FCSTD DOCUMENT  (FreeCAD 0.16R5861 (Git))
Label: extruder_mount_TAZ6_0.8
License: CC-BY 3.0
LicenseURL: http://creativecommons.org/licenses/by/3.0/
objects: Sketcher::SketchObject×85, PartDesign::Pocket×58, PartDesign::Pad×27, PartDesign::Chamfer×23, PartDesign::Fillet×17, Part::Feature×7
note: 302 computed .brp shape members not serialized (recipe doc carries the construction recipe); baked Part::Feature solids carry a one-line shape summary decoded from their .brp

FEATURE [Sketcher::SketchObject] Sketch
  sketch-geometry (38):
    g0: LineSegment [constr] StartX=-50 StartY=41.5 StartZ=0 EndX=50 EndY=41.5 EndZ=0
    g1: LineSegment StartX=50 StartY=41.5 StartZ=0 EndX=50 EndY=-41.5 EndZ=0
    g2: LineSegment [constr] StartX=50 StartY=-41.5 StartZ=0 EndX=-50 EndY=-41.5 EndZ=0
    g3: LineSegment StartX=-50 StartY=-41.5 StartZ=0 EndX=-50 EndY=41.5 EndZ=0
    g4: LineSegment StartX=-44 StartY=-41.5 StartZ=0 EndX=-45.4867 EndY=-53.8036 EndZ=0
    g5: LineSegment StartX=44 StartY=-41.5 StartZ=0 EndX=45.4867 EndY=-53.8036 EndZ=0
    g6: LineSegment StartX=45.4867 StartY=-53.8036 StartZ=0 EndX=0 EndY=-59.3 EndZ=0
    g7: LineSegment StartX=0 StartY=-59.3 StartZ=0 EndX=-45.4867 EndY=-53.8036 EndZ=0
    g8: LineSegment StartX=-50 StartY=-41.5 StartZ=0 EndX=-44 EndY=-41.5 EndZ=0
    g9: LineSegment StartX=44 StartY=-41.5 StartZ=0 EndX=50 EndY=-41.5 EndZ=0
    g10: LineSegment [constr] StartX=12.5 StartY=41.5 StartZ=0 EndX=12.5 EndY=51.1 EndZ=0
    g11: LineSegment [constr] StartX=12.5 StartY=51.1 StartZ=0 EndX=-12.5 EndY=51.1 EndZ=0
    g12: LineSegment [constr] StartX=-12.5 StartY=51.1 StartZ=0 EndX=-12.5 EndY=41.5 EndZ=0
    g13: ArcOfCircle CenterX=0 CenterY=44.7952 CenterZ=0 NormalX=0 NormalY=0 NormalZ=1 Radius=14 StartAngle=0.467146 EndAngle=2.67445
    g14: LineSegment [constr] StartX=-2.1 StartY=52.1 StartZ=0 EndX=2.1 EndY=52.1 EndZ=0
    g15: LineSegment StartX=2.1 StartY=52.1 StartZ=0 EndX=2.1 EndY=49.1 EndZ=0
    g16: LineSegment [constr] StartX=2.1 StartY=49.1 StartZ=0 EndX=-2.1 EndY=49.1 EndZ=0
    g17: LineSegment StartX=-2.1 StartY=49.1 StartZ=0 EndX=-2.1 EndY=52.1 EndZ=0
    g18: ArcOfCircle CenterX=0 CenterY=52.1 CenterZ=0 NormalX=0 NormalY=0 NormalZ=1 Radius=2.1 StartAngle=0 EndAngle=3.14159
    g19: ArcOfCircle CenterX=0 CenterY=49.1 CenterZ=0 NormalX=0 NormalY=0 NormalZ=1 Radius=2.1 StartAngle=3.14159 EndAngle=6.28319
    g20: ArcOfCircle CenterX=-15.5 CenterY=44.5 CenterZ=0 NormalX=0 NormalY=0 NormalZ=1 Radius=3 StartAngle=4.71239 EndAngle=6.28319
    g21: ArcOfCircle CenterX=15.5 CenterY=44.5 CenterZ=0 NormalX=0 NormalY=0 NormalZ=1 Radius=3 StartAngle=3.14159 EndAngle=4.71239
    g22: LineSegment StartX=-50 StartY=41.5 StartZ=0 EndX=-15.5 EndY=41.5 EndZ=0
    g23: LineSegment StartX=15.5 StartY=41.5 StartZ=0 EndX=50 EndY=41.5 EndZ=0
    g24: LineSegment StartX=-12.5 StartY=51.1 StartZ=0 EndX=-12.5 EndY=44.5 EndZ=0
    g25: LineSegment StartX=12.5 StartY=51.1 StartZ=0 EndX=12.5 EndY=44.5 EndZ=0
    g26: LineSegment [constr] StartX=-36 StartY=-13.5 StartZ=0 EndX=-8 EndY=-13.5 EndZ=0
    g27: LineSegment StartX=-8 StartY=-13.5 StartZ=0 EndX=-8 EndY=16.5 EndZ=0
    g28: LineSegment [constr] StartX=-8 StartY=16.5 StartZ=0 EndX=-36 EndY=16.5 EndZ=0
    g29: LineSegment StartX=-36 StartY=16.5 StartZ=0 EndX=-36 EndY=-13.5 EndZ=0
    g30: LineSegment [constr] StartX=8 StartY=16.5 StartZ=0 EndX=36 EndY=16.5 EndZ=0
    g31: LineSegment StartX=36 StartY=16.5 StartZ=0 EndX=36 EndY=-13.5 EndZ=0
    g32: LineSegment [constr] StartX=36 StartY=-13.5 StartZ=0 EndX=8 EndY=-13.5 EndZ=0
    g33: LineSegment StartX=8 StartY=-13.5 StartZ=0 EndX=8 EndY=16.5 EndZ=0
    g34: ArcOfCircle CenterX=-22 CenterY=16.5 CenterZ=0 NormalX=0 NormalY=0 NormalZ=1 Radius=14 StartAngle=0 EndAngle=3.14159
    g35: ArcOfCircle CenterX=22 CenterY=16.5 CenterZ=0 NormalX=0 NormalY=0 NormalZ=1 Radius=14 StartAngle=0 EndAngle=3.14159
    g36: ArcOfCircle CenterX=-22 CenterY=-13.5 CenterZ=0 NormalX=0 NormalY=0 NormalZ=1 Radius=14 StartAngle=3.14159 EndAngle=6.28319
    g37: ArcOfCircle CenterX=22 CenterY=-13.5 CenterZ=0 NormalX=0 NormalY=0 NormalZ=1 Radius=14 StartAngle=3.14159 EndAngle=6.28319
  constraints (114):
    c: Coincident(g0,g1)
    c: Coincident(g1,g2)
    c: Coincident(g2,g3)
    c: Coincident(g3,g0)
    c: Horizontal(g0)
    c: Horizontal(g2)
    c: Vertical(g1)
    c: Vertical(g3)
    c: DistanceX(g2) = -100
    c: DistanceY(g3) = 83
    c: Symmetric(g2,g1,g-2)
    c: Symmetric(g0,g2,g-1)
    c: PointOnObject(g4,g2)
    c: PointOnObject(g5,g2)
    c: Coincident(g5,g6)
    c: PointOnObject(g6,g-2)
    c: Coincident(g6,g7)
    c: Coincident(g7,g4)
    c: Perpendicular(g7,g4)
    c: Perpendicular(g5,g6)
    c: Equal(g5,g4)
    c: Angle(g6,g7) = 2.90109
    c: DistanceX(g5,g1) = 6
    c: DistanceX(g4,g2) = -6
    c: DistanceY(g6,g2) = 17.8
    c: Coincident(g8,g2)
    c: Coincident(g8,g4)
    c: Coincident(g9,g5)
    c: Coincident(g9,g1)
    c: Coincident(g10,g11)
    c: Coincident(g11,g12)
    c: Horizontal(g11)
    c: Vertical(g10)
    c: Vertical(g12)
    c: PointOnObject(g12,g0)
    c: PointOnObject(g10,g0)
    c: Symmetric(g11,g10,g-2)
    c: Coincident(g13,g11)
    c: Coincident(g13,g10)
    c: Radius(g13) = 14
    c: DistanceY(g11,g2) = -92.6
    c: DistanceX(g11) = -25
    c: Coincident(g14,g15)
    c: Coincident(g15,g16)
    c: Coincident(g16,g17)
    c: Coincident(g17,g14)
    c: Horizontal(g14)
    c: Horizontal(g16)
    c: Vertical(g15)
    c: Vertical(g17)
    c: PointOnObject(g18,g14)
    c: Coincident(g18,g14)
    c: Coincident(g18,g14)
    c: PointOnObject(g18,g-2)
    c: PointOnObject(g19,g16)
    c: Coincident(g19,g16)
    c: Coincident(g19,g15)
    c: Radius(g18) = 2.1
    c: DistanceY(g15) = -3
    c: DistanceY(g18,g11) = -1
    c: PointOnObject(g20,g12)
    c: PointOnObject(g20,g0)
    c: Tangent(g20,g0)
    c: Tangent(g20,g12)
    c: Radius(g20) = 3
    c: PointOnObject(g21,g10)
    c: PointOnObject(g21,g0)
    c: Tangent(g21,g0)
    c: Tangent(g10,g21)
    c: Equal(g20,g21)
    c: Coincident(g22,g0)
    c: Coincident(g23,g21)
    c: Coincident(g23,g0)
    c: Coincident(g22,g20)
    c: Coincident(g25,g21)
    c: Coincident(g10,g25)
    c: Coincident(g24,g11)
    c: Coincident(g24,g20)
    c: Coincident(g26,g27)
    c: Coincident(g27,g28)
    c: Coincident(g28,g29)
    c: Coincident(g29,g26)
    c: Horizontal(g26)
    c: Horizontal(g28)
    c: Vertical(g27)
    c: Vertical(g29)
    c: Coincident(g30,g31)
    c: Coincident(g31,g32)
    c: Coincident(g32,g33)
    c: Coincident(g33,g30)
    c: Horizontal(g30)
    c: Horizontal(g32)
    c: Vertical(g31)
    c: Vertical(g33)
    c: PointOnObject(g26,g32)
    c: PointOnObject(g30,g28)
    c: PointOnObject(g34,g28)
    c: Coincident(g34,g28)
    c: Coincident(g34,g27)
    c: Radius(g34) = 14
    c: DistanceY(g27) = 30
    c: DistanceX(g34,g0) = -28
    c: PointOnObject(g35,g30)
    c: Coincident(g35,g30)
    c: Coincident(g35,g30)
    c: Radius(g35) = 14
    c: DistanceX(g35,g0) = 28
    c: PointOnObject(g36,g26)
    c: Coincident(g36,g26)
    c: Coincident(g36,g26)
    c: DistanceY(g36,g2) = -28
    c: Coincident(g37,g32)
    c: Coincident(g37,g31)
    c: PointOnObject(g37,g32)
FEATURE [PartDesign::Pad] Pad
  Length = 6
  Length2 = 100
  Sketch = -> Sketch
  Type = 0
FEATURE [Sketcher::SketchObject] Sketch001
  ExternalGeometry = -> [Pad]
  Placement = pos=(-38.4641,4.61721,0) rot=(-0.531401,0.599005,0.599005;4.1185rad)
  Support = -> Pad [Face19]
  sketch-geometry (5):
    g0: LineSegment StartX=50.8773 StartY=8 StartZ=0 EndX=58.4773 EndY=0.4 EndZ=0
    g1: LineSegment StartX=58.4773 StartY=0.4 StartZ=0 EndX=58.4773 EndY=-2 EndZ=0
    g2: LineSegment StartX=50.8773 StartY=8 StartZ=0 EndX=60.8773 EndY=8 EndZ=0
    g3: LineSegment StartX=60.8773 StartY=8 StartZ=0 EndX=60.8773 EndY=-2 EndZ=0
    g4: LineSegment StartX=60.8773 StartY=-2 StartZ=0 EndX=58.4773 EndY=-2 EndZ=0
  constraints (15):
    c: Coincident(g1,g0)
    c: PointOnObject(g-3,g0)
    c: Angle(g-3,g0) = 0.785398
    c: Vertical(g1)
    c: Coincident(g2,g3)
    c: Coincident(g3,g4)
    c: Horizontal(g2)
    c: Horizontal(g4)
    c: Vertical(g3)
    c: Coincident(g4,g1)
    c: Coincident(g2,g0)
    c: DistanceY(g-3,g2) = 2
    c: DistanceY(g-3,g3) = -2
    c: DistanceX(g-3,g2) = 2
    c: DistanceX(g0,g-3) = 0.4
FEATURE [PartDesign::Pocket] Pocket
  Length = 5
  Sketch = -> Sketch001
  Type = 1
FEATURE [Sketcher::SketchObject] Sketch002
  ExternalGeometry = -> [Pocket]
  Placement = pos=(38.4641,4.61721,0) rot=(0.531401,0.599005,0.599005;2.16469rad)
  Support = -> Pocket [Face20]
  sketch-geometry (5):
    g0: LineSegment StartX=-58.4773 StartY=0.4 StartZ=0 EndX=-50.8773 EndY=8 EndZ=0
    g1: LineSegment StartX=-50.8773 StartY=8 StartZ=0 EndX=-60.8773 EndY=8 EndZ=0
    g2: LineSegment StartX=-60.8773 StartY=8 StartZ=0 EndX=-60.8773 EndY=-2 EndZ=0
    g3: LineSegment StartX=-60.8773 StartY=-2 StartZ=0 EndX=-58.4773 EndY=-2 EndZ=0
    g4: LineSegment StartX=-58.4773 StartY=0.4 StartZ=0 EndX=-58.4773 EndY=-2 EndZ=0
  constraints (15):
    c: Coincident(g1,g2)
    c: Coincident(g2,g3)
    c: Horizontal(g1)
    c: Horizontal(g3)
    c: Vertical(g2)
    c: Coincident(g1,g0)
    c: Coincident(g4,g0)
    c: Coincident(g4,g3)
    c: Vertical(g4)
    c: DistanceX(g-3,g0) = 0.4
    c: DistanceY(g-3,g2) = -2
    c: DistanceX(g2,g-3) = 2
    c: DistanceY(g-3,g1) = 2
    c: Angle(g0,g-3) = 0.785398
    c: PointOnObject(g-3,g0)
FEATURE [PartDesign::Pocket] Pocket001
  Length = 5
  Sketch = -> Sketch002
  Type = 1
FEATURE [Sketcher::SketchObject] Sketch003
  ExternalGeometry = -> [Pocket001]
  Placement = pos=(0,0,6) rot=(0,0,1;0rad)
  Support = -> Pocket001 [Face5]
  sketch-geometry (8):
    g0: LineSegment StartX=-50 StartY=41.5 StartZ=0 EndX=-44 EndY=41.5 EndZ=0
    g1: LineSegment StartX=-44 StartY=41.5 StartZ=0 EndX=-44 EndY=-33.5 EndZ=0
    g2: LineSegment StartX=-50 StartY=-41.5 StartZ=0 EndX=-50 EndY=41.5 EndZ=0
    g3: LineSegment StartX=44 StartY=-33.5 StartZ=0 EndX=-44 EndY=-33.5 EndZ=0
    g4: LineSegment StartX=-50 StartY=-41.5 StartZ=0 EndX=50 EndY=-41.5 EndZ=0
    g5: LineSegment StartX=44 StartY=-8.5 StartZ=0 EndX=50 EndY=-8.5 EndZ=0
    g6: LineSegment StartX=50 StartY=-8.5 StartZ=0 EndX=50 EndY=-41.5 EndZ=0
    g7: LineSegment StartX=44 StartY=-33.5 StartZ=0 EndX=44 EndY=-8.5 EndZ=0
  constraints (22):
    c: Coincident(g0,g1)
    c: Coincident(g2,g0)
    c: Horizontal(g0)
    c: Vertical(g1)
    c: Vertical(g2)
    c: Coincident(g0,g-3)
    c: Horizontal(g3)
    c: Horizontal(g4)
    c: Coincident(g4,g2)
    c: Coincident(g1,g3)
    c: Coincident(g5,g6)
    c: Coincident(g7,g5)
    c: Horizontal(g5)
    c: Vertical(g6)
    c: Vertical(g7)
    c: Coincident(g3,g7)
    c: Coincident(g4,g6)
    c: Coincident(g-4,g4)
    c: DistanceY(g5,g4) = -33
    c: DistanceX(g5) = 6
    c: DistanceY(g3,g4) = -8
    c: DistanceX(g0) = 6
FEATURE [PartDesign::Pad] Pad001
  Length = 30
  Length2 = 100
  Sketch = -> Sketch003
  Type = 0
FEATURE [Sketcher::SketchObject] Sketch004
  ExternalGeometry = -> [Pad001]
  Placement = pos=(-50,0,0) rot=(0.57735,-0.57735,-0.57735;2.0944rad)
  Support = -> Pad001 [Face37]
  sketch-geometry (5):
    g0: ArcOfCircle CenterX=-54.7978 CenterY=120.229 CenterZ=0 NormalX=0 NormalY=0 NormalZ=1 Radius=115 StartAngle=4.82828 EndAngle=5.46131
    g1: LineSegment [constr] StartX=23.5 StartY=36 StartZ=0 EndX=41.5 EndY=36 EndZ=0
    g2: LineSegment StartX=-41.5 StartY=6 StartZ=0 EndX=-51.5 EndY=46 EndZ=0
    g3: LineSegment StartX=-51.5 StartY=46 StartZ=0 EndX=23.5 EndY=46 EndZ=0
    g4: LineSegment StartX=23.5 StartY=46 StartZ=0 EndX=23.5 EndY=36 EndZ=0
  constraints (14):
    c: Coincident(g0,g-3)
    c: Coincident(g1,g0)
    c: Coincident(g1,g-4)
    c: Horizontal(g1)
    c: DistanceX(g1) = 18
    c: Radius(g0) = 115
    c: Coincident(g2,g0)
    c: Coincident(g2,g3)
    c: Horizontal(g3)
    c: Coincident(g3,g4)
    c: Coincident(g4,g0)
    c: Vertical(g4)
    c: DistanceY(g4) = -10
    c: DistanceX(g-3,g2) = -10
FEATURE [PartDesign::Pocket] Pocket002
  Length = 5
  Sketch = -> Sketch004
  Type = 1
FEATURE [Sketcher::SketchObject] Sketch005
  ExternalGeometry = -> [Pocket002]
  Placement = pos=(0,0,36) rot=(0,0,1;0rad)
  Support = -> Pocket002 [Face42]
  sketch-geometry (4):
    g0: LineSegment StartX=-50 StartY=-33.5 StartZ=0 EndX=50 EndY=-33.5 EndZ=0
    g1: LineSegment StartX=50 StartY=-33.5 StartZ=0 EndX=50 EndY=-41.5 EndZ=0
    g2: LineSegment StartX=50 StartY=-41.5 StartZ=0 EndX=-50 EndY=-41.5 EndZ=0
    g3: LineSegment StartX=-50 StartY=-41.5 StartZ=0 EndX=-50 EndY=-33.5 EndZ=0
  constraints (11):
    c: Coincident(g0,g1)
    c: Coincident(g1,g2)
    c: Coincident(g2,g3)
    c: Coincident(g3,g0)
    c: Horizontal(g0)
    c: Horizontal(g2)
    c: Vertical(g1)
    c: Vertical(g3)
    c: Coincident(g1,g-3)
    c: Coincident(g2,g-3)
    c: PointOnObject(g-4,g0)
FEATURE [PartDesign::Pad] Pad002
  Length = 19.5
  Length2 = 100
  Sketch = -> Sketch005
  Type = 0
FEATURE [Sketcher::SketchObject] Sketch006
  ExternalGeometry = -> [Pad002]
  Placement = pos=(0,-41.5,0) rot=(1,0,0;1.5708rad)
  Support = -> Pad002 [Face42]
  sketch-geometry (5):
    g0: ArcOfCircle CenterX=-8.25 CenterY=40.4 CenterZ=0 NormalX=0 NormalY=0 NormalZ=1 Radius=21 StartAngle=3.14159 EndAngle=6.28319
    g1: LineSegment StartX=-29.25 StartY=65.4 StartZ=0 EndX=12.75 EndY=65.4 EndZ=0
    g2: LineSegment StartX=12.75 StartY=65.4 StartZ=0 EndX=12.75 EndY=40.4 EndZ=0
    g3: LineSegment [constr] StartX=12.75 StartY=40.4 StartZ=0 EndX=-29.25 EndY=40.4 EndZ=0
    g4: LineSegment StartX=-29.25 StartY=40.4 StartZ=0 EndX=-29.25 EndY=65.4 EndZ=0
  constraints (15):
    c: Coincident(g1,g2)
    c: Coincident(g2,g3)
    c: Coincident(g3,g4)
    c: Coincident(g4,g1)
    c: Horizontal(g1)
    c: Horizontal(g3)
    c: Vertical(g2)
    c: Vertical(g4)
    c: Coincident(g2,g0)
    c: Coincident(g0,g3)
    c: PointOnObject(g0,g3)
    c: DistanceX(g3) = -42
    c: DistanceY(g0,g-3) = -4.4
    c: DistanceX(g0,g-3) = -20.75
    c: DistanceY(g4) = 25
FEATURE [PartDesign::Pocket] Pocket003
  Length = 9
  Sketch = -> Sketch006
  Type = 0
FEATURE [Sketcher::SketchObject] Sketch007
  ExternalGeometry = -> [Pocket003]
  Placement = pos=(0,-41.5,0) rot=(1,0,0;1.5708rad)
  Support = -> Pocket003 [Face44]
  sketch-geometry (6):
    g0: ArcOfCircle CenterX=-37.25 CenterY=48.4 CenterZ=0 NormalX=0 NormalY=0 NormalZ=1 Radius=7.1 StartAngle=1.5708 EndAngle=2.75292
    g1: LineSegment StartX=-43.8204 StartY=51.0906 StartZ=0 EndX=-50 EndY=36 EndZ=0
    g2: LineSegment StartX=-56 StartY=61.5 StartZ=0 EndX=-37.25 EndY=61.5 EndZ=0
    g3: LineSegment StartX=-37.25 StartY=61.5 StartZ=0 EndX=-37.25 EndY=55.5 EndZ=0
    g4: LineSegment StartX=-50 StartY=36 StartZ=0 EndX=-56 EndY=36 EndZ=0
    g5: LineSegment StartX=-56 StartY=36 StartZ=0 EndX=-56 EndY=61.5 EndZ=0
  constraints (18):
    c: PointOnObject(g0,g-4)
    c: DistanceX(g0,g-4) = -12.75
    c: DistanceY(g-5,g0) = 12.4
    c: Tangent(g-4,g0)
    c: Coincident(g1,g0)
    c: Coincident(g1,g-5)
    c: Tangent(g1,g0)
    c: Coincident(g2,g3)
    c: Coincident(g4,g5)
    c: Coincident(g5,g2)
    c: Horizontal(g2)
    c: Horizontal(g4)
    c: Vertical(g3)
    c: Vertical(g5)
    c: Coincident(g0,g3)
    c: Coincident(g4,g1)
    c: DistanceX(g4) = -6
    c: DistanceY(g3) = -6
FEATURE [PartDesign::Pocket] Pocket004
  Length = 10
  Sketch = -> Sketch007
  Type = 0
FEATURE [Sketcher::SketchObject] Sketch008
  ExternalGeometry = -> [Pocket004]
  Placement = pos=(0,-41.5,0) rot=(1,0,0;1.5708rad)
  Support = -> Pocket004 [Face44]
  sketch-geometry (6):
    g0: ArcOfCircle CenterX=27.75 CenterY=48.4 CenterZ=0 NormalX=0 NormalY=0 NormalZ=1 Radius=7.1 StartAngle=0.77988 EndAngle=1.5708
    g1: LineSegment StartX=32.7981 StartY=53.3927 StartZ=0 EndX=50 EndY=36 EndZ=0
    g2: LineSegment StartX=50 StartY=36 StartZ=0 EndX=56 EndY=36 EndZ=0
    g3: LineSegment StartX=56 StartY=36 StartZ=0 EndX=56 EndY=61.5 EndZ=0
    g4: LineSegment StartX=56 StartY=61.5 StartZ=0 EndX=27.75 EndY=61.5 EndZ=0
    g5: LineSegment StartX=27.75 StartY=61.5 StartZ=0 EndX=27.75 EndY=55.5 EndZ=0
  constraints (18):
    c: PointOnObject(g0,g-3)
    c: Coincident(g1,g0)
    c: Coincident(g1,g-4)
    c: Tangent(g0,g1)
    c: Tangent(g0,g-3)
    c: DistanceY(g0,g1) = -12.4
    c: DistanceX(g0,g-3) = 22.25
    c: Coincident(g2,g3)
    c: Coincident(g3,g4)
    c: Coincident(g4,g5)
    c: Horizontal(g2)
    c: Horizontal(g4)
    c: Vertical(g3)
    c: Vertical(g5)
    c: Coincident(g1,g2)
    c: Coincident(g5,g0)
    c: DistanceY(g5) = -6
    c: DistanceX(g2) = 6
FEATURE [PartDesign::Pocket] Pocket005
  Length = 10
  Sketch = -> Sketch008
  Type = 0
FEATURE [Sketcher::SketchObject] Sketch009
  ExternalGeometry = -> [Pocket005]
  Placement = pos=(0,-41.5,0) rot=(1,0,0;1.5708rad)
  Support = -> Pocket005 [Face42]
  sketch-geometry (6):
    g0: ArcOfCircle CenterX=-33.25 CenterY=40.4 CenterZ=0 NormalX=0 NormalY=0 NormalZ=1 Radius=6 StartAngle=3.14159 EndAngle=4.71239
    g1: LineSegment StartX=-39.25 StartY=70.4 StartZ=0 EndX=22.75 EndY=70.4 EndZ=0
    g2: LineSegment StartX=22.75 StartY=70.4 StartZ=0 EndX=22.75 EndY=40.4 EndZ=0
    g3: LineSegment StartX=16.75 StartY=34.4 StartZ=0 EndX=-33.25 EndY=34.4 EndZ=0
    g4: LineSegment StartX=-39.25 StartY=40.4 StartZ=0 EndX=-39.25 EndY=70.4 EndZ=0
    g5: ArcOfCircle CenterX=16.75 CenterY=40.4 CenterZ=0 NormalX=0 NormalY=0 NormalZ=1 Radius=6 StartAngle=4.71239 EndAngle=6.28319
  constraints (20):
    c: Coincident(g1,g2)
    c: Coincident(g4,g1)
    c: Horizontal(g1)
    c: Horizontal(g3)
    c: Vertical(g2)
    c: Vertical(g4)
    c: Coincident(g0,g3)
    c: Coincident(g4,g0)
    c: Coincident(g5,g3)
    c: Coincident(g5,g2)
    c: Tangent(g5,g3)
    c: Tangent(g5,g2)
    c: Tangent(g0,g3)
    c: Tangent(g4,g0)
    c: Radius(g0) = 6
    c: Radius(g5) = 6
    c: DistanceY(g-3,g0) = 4.4
    c: DistanceX(g0,g-3) = -16.75
    c: DistanceX(g5,g0) = -50
    c: DistanceY(g2) = -30
FEATURE [PartDesign::Pocket] Pocket006
  Length = 2.1
  Sketch = -> Sketch009
  Type = 0
FEATURE [Sketcher::SketchObject] Sketch010
  ExternalGeometry = -> [Pocket006]
  Placement = pos=(0,-39.4,0) rot=(1,0,0;1.5708rad)
  Support = -> Pocket006 [Face62]
  sketch-geometry (1):
    g0: Circle CenterX=-33.25 CenterY=40.4 CenterZ=0 NormalX=0 NormalY=0 NormalZ=1 Radius=2.5
  constraints (2):
    c: Coincident(g0,g-3)
    c: Radius(g0) = 2.5
FEATURE [PartDesign::Pocket] Pocket007
  Length = 7
  Sketch = -> Sketch010
  Type = 0
FEATURE [Sketcher::SketchObject] Sketch011
  ExternalGeometry = -> [Pocket007]
  Placement = pos=(0,-39.4,0) rot=(1,0,0;1.5708rad)
  Support = -> Pocket007 [Face59]
  sketch-geometry (1):
    g0: Circle CenterX=16.75 CenterY=40.4 CenterZ=0 NormalX=0 NormalY=0 NormalZ=1 Radius=2.5
  constraints (2):
    c: Coincident(g0,g-3)
    c: Radius(g0) = 2.5
FEATURE [PartDesign::Pocket] Pocket008
  Length = 5
  Sketch = -> Sketch011
  Type = 0
FEATURE [Sketcher::SketchObject] Sketch012
  ExternalGeometry = -> [Pocket008]
  Placement = pos=(0,0,0) rot=(1,0,0;3.14159rad)
  Support = -> Pocket008 [Face4]
  sketch-geometry (8):
    g0: LineSegment StartX=-44 StartY=41.5 StartZ=0 EndX=-54 EndY=41.5 EndZ=0
    g1: LineSegment StartX=-54 StartY=41.5 StartZ=0 EndX=-54 EndY=76.5 EndZ=0
    g2: LineSegment StartX=-44 StartY=66.5 StartZ=0 EndX=-44 EndY=41.5 EndZ=0
    g3: LineSegment StartX=44 StartY=41.5 StartZ=0 EndX=54 EndY=41.5 EndZ=0
    g4: LineSegment StartX=54 StartY=41.5 StartZ=0 EndX=54 EndY=76.5 EndZ=0
    g5: LineSegment StartX=44 StartY=66.5 StartZ=0 EndX=44 EndY=41.5 EndZ=0
    g6: LineSegment StartX=54 StartY=76.5 StartZ=0 EndX=-54 EndY=76.5 EndZ=0
    g7: LineSegment StartX=-44 StartY=66.5 StartZ=0 EndX=44 EndY=66.5 EndZ=0
  constraints (24):
    c: Coincident(g0,g1)
    c: Horizontal(g0)
    c: Vertical(g1)
    c: Vertical(g2)
    c: Coincident(g3,g4)
    c: Horizontal(g3)
    c: Vertical(g4)
    c: Vertical(g5)
    c: DistanceX(g3) = 10
    c: DistanceX(g0) = -10
    c: Horizontal(g6)
    c: Horizontal(g7)
    c: Coincident(g7,g2)
    c: Coincident(g6,g1)
    c: Coincident(g6,g4)
    c: Coincident(g7,g5)
    c: DistanceY(g2) = -25
    c: DistanceY(g1) = 35
    c: Coincident(g3,g5)
    c: PointOnObject(g3,g-4)
    c: DistanceX(g-4,g3) = -6
    c: Coincident(g0,g2)
    c: PointOnObject(g0,g-3)
    c: DistanceX(g-3,g0) = 6
FEATURE [PartDesign::Pocket] Pocket009
  Length = 6
  Sketch = -> Sketch012
  Type = 0
FEATURE [PartDesign::Fillet] Fillet
  Base = -> Pocket009 [Edge60]
  Radius = 5.99
FEATURE [PartDesign::Fillet] Fillet001
  Base = -> Fillet [Edge50]
  Radius = 5.99
FEATURE [PartDesign::Chamfer] Chamfer
  Base = -> Fillet001 [Edge13,Edge6]
  Size = 0.2
FEATURE [PartDesign::Chamfer] Chamfer001
  Base = -> Chamfer [Edge15,Edge14,Edge12,Edge10,Edge8,Edge6,Edge4]
  Size = 0.2
FEATURE [PartDesign::Chamfer] Chamfer002
  Base = -> Chamfer001 [Edge23,Edge20,Edge22,Edge21,Edge25,Edge24,Edge26,Edge27]
  Size = 0.2
FEATURE [PartDesign::Chamfer] Chamfer003
  Base = -> Chamfer002 [Edge21,Edge22,Edge20]
  Size = 0.4
FEATURE [Sketcher::SketchObject] Sketch013
  ExternalGeometry = -> [Chamfer003]
  Placement = pos=(0,-34.4,0) rot=(1,0,0;1.5708rad)
  Support = -> Chamfer003 [Face91]
  sketch-geometry (1):
    g0: Circle CenterX=16.75 CenterY=40.4 CenterZ=0 NormalX=0 NormalY=0 NormalZ=1 Radius=2.5
  constraints (2):
    c: Coincident(g0,g-3)
    c: Equal(g-3,g0)
FEATURE [PartDesign::Pocket] Pocket010
  Length = 5
  Sketch = -> Sketch013
  Type = 3
FEATURE [PartDesign::Chamfer] Chamfer004
  Base = -> Pocket010 [Edge229,Edge230]
  Size = 1
FEATURE [Sketcher::SketchObject] Sketch014
  Placement = pos=(0,0,55.5) rot=(0,0,1;0rad)
  Support = -> Chamfer002 [Face82]
  sketch-geometry (4):
    g0: LineSegment StartX=73.127 StartY=-81.5191 StartZ=0 EndX=-86.1333 EndY=-81.5191 EndZ=0
    g1: LineSegment StartX=-86.1333 StartY=-81.5191 StartZ=0 EndX=-86.1333 EndY=47.4059 EndZ=0
    g2: LineSegment StartX=-86.1333 StartY=47.4059 StartZ=0 EndX=73.127 EndY=47.4059 EndZ=0
    g3: LineSegment StartX=73.127 StartY=47.4059 StartZ=0 EndX=73.127 EndY=-81.5191 EndZ=0
  constraints (12):
    c: Coincident(g0,g1)
    c: Coincident(g1,g2)
    c: Coincident(g2,g3)
    c: Coincident(g3,g0)
    c: Horizontal(g0)
    c: Horizontal(g2)
    c: Vertical(g1)
    c: Vertical(g3)
    c: DistanceX(g0) = 73.127
    c: DistanceY(g0) = -81.5191
    c: DistanceX(g1) = -86.1333
    c: DistanceY(g1) = 47.4059
FEATURE [PartDesign::Pocket] Pocket011
  Length = 49.5
  Sketch = -> Sketch014
  Type = 0
FEATURE [Sketcher::SketchObject] Sketch015
  ExternalGeometry = -> [Pocket011]
  Placement = pos=(0,0,6) rot=(0,0,1;0rad)
  Support = -> Pocket011 [Face53]
  sketch-geometry (6):
    g0: LineSegment StartX=-40 StartY=-50.6154 StartZ=0 EndX=40 EndY=-50.6154 EndZ=0
    g1: LineSegment StartX=40 StartY=-50.6154 StartZ=0 EndX=40 EndY=-28.6154 EndZ=0
    g2: LineSegment StartX=40 StartY=-28.6154 StartZ=0 EndX=-40 EndY=-28.6154 EndZ=0
    g3: LineSegment StartX=-40 StartY=-28.6154 StartZ=0 EndX=-40 EndY=-50.6154 EndZ=0
    g4: LineSegment [constr] StartX=-40 StartY=-50.6154 StartZ=0 EndX=-50 EndY=-50.6154 EndZ=0
    g5: LineSegment [constr] StartX=40 StartY=-50.6154 StartZ=0 EndX=50 EndY=-50.6154 EndZ=0
  constraints (18):
    c: Coincident(g0,g1)
    c: Coincident(g1,g2)
    c: Coincident(g2,g3)
    c: Coincident(g3,g0)
    c: Horizontal(g0)
    c: Horizontal(g2)
    c: Vertical(g1)
    c: Vertical(g3)
    c: DistanceX(g2) = -80
    c: Coincident(g4,g0)
    c: PointOnObject(g4,g-4)
    c: Horizontal(g4)
    c: Coincident(g5,g0)
    c: PointOnObject(g5,g-5)
    c: Horizontal(g5)
    c: Equal(g4,g5)
    c: DistanceY(g-3,g0) = 3
    c: DistanceY(g-3,g2) = 25
FEATURE [PartDesign::Pad] Pad003  label="start_of_lancewood"
  Length = 50
  Length2 = 100
  Sketch = -> Sketch015
  Type = 0
FEATURE [Sketcher::SketchObject] Sketch016
  ExternalGeometry = -> [Pad003]
  Placement = pos=(-40,0,0) rot=(0.57735,-0.57735,-0.57735;2.0944rad)
  Support = -> Pad003 [Face56]
  sketch-geometry (4):
    g0: LineSegment StartX=28.6154 StartY=6 StartZ=0 EndX=43.6154 EndY=21 EndZ=0
    g1: LineSegment StartX=43.6154 StartY=21 StartZ=0 EndX=43.6154 EndY=56 EndZ=0
    g2: LineSegment StartX=43.6154 StartY=56 StartZ=0 EndX=28.6154 EndY=56 EndZ=0
    g3: LineSegment StartX=28.6154 StartY=56 StartZ=0 EndX=28.6154 EndY=6 EndZ=0
  constraints (10):
    c: Coincident(g-6,g0)
    c: Coincident(g0,g1)
    c: PointOnObject(g1,g-3)
    c: Vertical(g1)
    c: DistanceX(g-5,g1) = -7
    c: DistanceY(g-5,g0) = 15
    c: Coincident(g1,g2)
    c: Coincident(g2,g-6)
    c: Coincident(g2,g3)
    c: Coincident(g3,g0)
FEATURE [PartDesign::Pocket] Pocket012
  Length = 5
  Sketch = -> Sketch016
  Type = 1
FEATURE [Sketcher::SketchObject] Sketch017
  ExternalGeometry = -> [Pocket012]
  Placement = pos=(-40,0,0) rot=(0.57735,-0.57735,-0.57735;2.0944rad)
  Support = -> Pocket012 [Face56]
  sketch-geometry (3):
    g0: LineSegment StartX=50.6154 StartY=14 StartZ=0 EndX=42.6154 EndY=6 EndZ=0
    g1: LineSegment StartX=42.6154 StartY=6 StartZ=0 EndX=50.6154 EndY=6 EndZ=0
    g2: LineSegment StartX=50.6154 StartY=6 StartZ=0 EndX=50.6154 EndY=14 EndZ=0
  constraints (8):
    c: PointOnObject(g0,g-4)
    c: Coincident(g0,g1)
    c: Coincident(g1,g-4)
    c: Horizontal(g1)
    c: Coincident(g1,g2)
    c: Coincident(g2,g0)
    c: Parallel(g-5,g0)
    c: DistanceX(g0,g-5) = -14
FEATURE [PartDesign::Pocket] Pocket013
  Length = 5
  Sketch = -> Sketch017
  Type = 1
FEATURE [Sketcher::SketchObject] Sketch018
  ExternalGeometry = -> [Pocket013]
  Placement = pos=(0,0,6) rot=(0,0,1;0rad)
  Support = -> Pocket013 [Face57]
  sketch-geometry (3):
    g0: LineSegment StartX=0 StartY=-53.2569 StartZ=0 EndX=-40 EndY=-42.6154 EndZ=0
    g1: LineSegment StartX=0 StartY=-53.2569 StartZ=0 EndX=40 EndY=-42.6154 EndZ=0
    g2: LineSegment StartX=-40 StartY=-42.6154 StartZ=0 EndX=40 EndY=-42.6154 EndZ=0
  constraints (6):
    c: Coincident(g-4,g0)
    c: Coincident(g0,g-5)
    c: Coincident(g-3,g1)
    c: Coincident(g1,g-5)
    c: Coincident(g2,g0)
    c: Coincident(g2,g1)
FEATURE [PartDesign::Pad] Pad004
  Length = 10
  Length2 = 100
  Sketch = -> Sketch018
  Type = 0
FEATURE [PartDesign::Chamfer] Chamfer005
  Base = -> Pad004 [Edge195,Edge186]
  Size = 2.5
FEATURE [Sketcher::SketchObject] Sketch019
  ExternalGeometry = -> [Chamfer005]
  Placement = pos=(0,0,56) rot=(0,0,1;0rad)
  Support = -> Chamfer005 [Face20]
  sketch-geometry (1):
    g0: Circle CenterX=5 CenterY=-3.5 CenterZ=0 NormalX=0 NormalY=0 NormalZ=1 Radius=38
  constraints (3):
    c: Radius(g0) = 38
    c: DistanceX(g0,g-3) = -55
    c: DistanceY(g-3,g0) = -45
FEATURE [PartDesign::Pocket] Pocket014
  Length = 48
  Sketch = -> Sketch019
  Type = 0
FEATURE [Part::Feature] Pocket014001  label="Pocket015"
  shape: bbox 100 x 117.7 x 56 mm, 65 faces (baked)
FEATURE [PartDesign::Fillet] Fillet002
  Base = -> Pocket014001 [Edge142,Edge146]
  Radius = 3
FEATURE [Sketcher::SketchObject] Sketch020
  ExternalGeometry = -> [Fillet002]
  Placement = pos=(0,-43.6154,0) rot=(0,0.707107,0.707107;3.14159rad)
  Support = -> Fillet002 [Face43]
  sketch-geometry (8):
    g0: ArcOfCircle CenterX=0 CenterY=56 CenterZ=0 NormalX=0 NormalY=0 NormalZ=1 Radius=13.5 StartAngle=0 EndAngle=3.14159
    g1: ArcOfCircle CenterX=0 CenterY=39 CenterZ=0 NormalX=0 NormalY=0 NormalZ=1 Radius=13.5 StartAngle=3.14159 EndAngle=6.28319
    g2: LineSegment StartX=-13.5 StartY=56 StartZ=0 EndX=-13.5 EndY=39 EndZ=0
    g3: LineSegment StartX=13.5 StartY=56 StartZ=0 EndX=13.5 EndY=39 EndZ=0
    g4: LineSegment [constr] StartX=-25 StartY=39 StartZ=0 EndX=0 EndY=39 EndZ=0
    g5: LineSegment [constr] StartX=0 StartY=39 StartZ=0 EndX=25 EndY=39 EndZ=0
    g6: Circle CenterX=-25 CenterY=39 CenterZ=0 NormalX=0 NormalY=0 NormalZ=1 Radius=2.75
    g7: Circle CenterX=25 CenterY=39 CenterZ=0 NormalX=0 NormalY=0 NormalZ=1 Radius=2.75
  constraints (20):
    c: Tangent(g0,g3) = 1.5708
    c: Tangent(g0,g2) = -1.5708
    c: Tangent(g2,g1) = -1.5708
    c: Tangent(g3,g1) = 1.5708
    c: Vertical(g2)
    c: Equal(g0,g1)
    c: PointOnObject(g0,g-5)
    c: PointOnObject(g0,g-2)
    c: Radius(g0) = 13.5
    c: Coincident(g4,g1)
    c: Horizontal(g4)
    c: Coincident(g5,g1)
    c: Horizontal(g5)
    c: Equal(g5,g4)
    c: DistanceX(g4,g5) = 50
    c: Coincident(g6,g4)
    c: Coincident(g7,g5)
    c: Radius(g7) = 2.75
    c: Equal(g7,g6)
    c: DistanceY(g-6,g1) = 33
FEATURE [PartDesign::Pocket] Pocket014002
  Length = 5
  Sketch = -> Sketch020
  Type = 1
FEATURE [Sketcher::SketchObject] Sketch021
  ExternalGeometry = -> [Pocket014002]
  Placement = pos=(0,0,56) rot=(0,0,1;0rad)
  Support = -> Pocket014002 [Face74]
  sketch-geometry (16):
    g0: LineSegment StartX=-35.9585 StartY=-43.6154 StartZ=0 EndX=-40 EndY=-50.6154 EndZ=0
    g1: LineSegment [constr] StartX=-40 StartY=-50.6154 StartZ=0 EndX=-40 EndY=-43.6154 EndZ=0
    g2: LineSegment [constr] StartX=-40 StartY=-43.6154 StartZ=0 EndX=-35.9585 EndY=-43.6154 EndZ=0
    g3: LineSegment StartX=40 StartY=-50.6154 StartZ=0 EndX=35.9585 EndY=-43.6154 EndZ=0
    g4: LineSegment [constr] StartX=35.9585 StartY=-43.6154 StartZ=0 EndX=40 EndY=-43.6154 EndZ=0
    g5: LineSegment [constr] StartX=40 StartY=-43.6154 StartZ=0 EndX=40 EndY=-50.6154 EndZ=0
    g6: LineSegment StartX=-35.9585 StartY=-43.6154 StartZ=0 EndX=-40 EndY=-36.6154 EndZ=0
    g7: LineSegment [constr] StartX=-40 StartY=-36.6154 StartZ=0 EndX=-40 EndY=-43.6154 EndZ=0
    g8: LineSegment StartX=35.9585 StartY=-43.6154 StartZ=0 EndX=40 EndY=-36.6154 EndZ=0
    g9: LineSegment [constr] StartX=40 StartY=-36.6154 StartZ=0 EndX=40 EndY=-43.6154 EndZ=0
    g10: LineSegment StartX=-40 StartY=-36.6154 StartZ=0 EndX=-45 EndY=-36.6154 EndZ=0
    g11: LineSegment StartX=-45 StartY=-36.6154 StartZ=0 EndX=-45 EndY=-50.6154 EndZ=0
    g12: LineSegment StartX=-45 StartY=-50.6154 StartZ=0 EndX=-40 EndY=-50.6154 EndZ=0
    g13: LineSegment StartX=40 StartY=-36.6154 StartZ=0 EndX=45 EndY=-36.6154 EndZ=0
    g14: LineSegment StartX=45 StartY=-36.6154 StartZ=0 EndX=45 EndY=-50.6154 EndZ=0
    g15: LineSegment StartX=45 StartY=-50.6154 StartZ=0 EndX=40 EndY=-50.6154 EndZ=0
  constraints (41):
    c: Coincident(g0,g-4)
    c: Coincident(g0,g1)
    c: Vertical(g1)
    c: Coincident(g1,g2)
    c: Coincident(g2,g0)
    c: Horizontal(g2)
    c: Angle(g2,g0) = 1.0472
    c: Coincident(g1,g-3)
    c: Coincident(g-6,g3)
    c: Coincident(g3,g4)
    c: Coincident(g4,g5)
    c: Coincident(g5,g3)
    c: Equal(g3,g0)
    c: Coincident(g4,g-5)
    c: Horizontal(g4)
    c: Coincident(g0,g6)
    c: Coincident(g6,g7)
    c: Coincident(g7,g1)
    c: Vertical(g7)
    c: Coincident(g3,g8)
    c: Coincident(g8,g9)
    c: Coincident(g9,g4)
    c: Vertical(g9)
    c: Equal(g9,g7)
    c: Equal(g7,g-3)
    c: Coincident(g10,g11)
    c: Coincident(g11,g12)
    c: Horizontal(g10)
    c: Horizontal(g12)
    c: Vertical(g11)
    c: Coincident(g10,g6)
    c: Coincident(g13,g14)
    c: Coincident(g14,g15)
    c: Horizontal(g13)
    c: Horizontal(g15)
    c: Vertical(g14)
    c: Coincident(g13,g8)
    c: Coincident(g15,g3)
    c: Coincident(g0,g12)
    c: Equal(g10,g13)
    c: DistanceX(g13) = 5
FEATURE [PartDesign::Pocket] Pocket014003
  Length = 50
  Sketch = -> Sketch021
  Type = 0
FEATURE [PartDesign::Chamfer] Chamfer006
  Base = -> Pocket014003 [Edge209,Edge222]
  Size = 3
FEATURE [Sketcher::SketchObject] Sketch022
  ExternalGeometry = -> [Chamfer006]
  Placement = pos=(0,-43.6154,0) rot=(0,0.707107,0.707107;3.14159rad)
  Support = -> Chamfer006 [Face6]
  sketch-geometry (6):
    g0: LineSegment StartX=-40 StartY=56 StartZ=0 EndX=-13.5 EndY=56 EndZ=0
    g1: LineSegment StartX=-13.5 StartY=56 StartZ=0 EndX=-13.5 EndY=43.6428 EndZ=0
    g2: LineSegment StartX=-13.5 StartY=43.6428 StartZ=0 EndX=-40 EndY=56 EndZ=0
    g3: LineSegment StartX=40 StartY=56 StartZ=0 EndX=13.5 EndY=43.6428 EndZ=0
    g4: LineSegment StartX=13.5 StartY=43.6428 StartZ=0 EndX=13.5 EndY=56 EndZ=0
    g5: LineSegment StartX=13.5 StartY=56 StartZ=0 EndX=40 EndY=56 EndZ=0
  constraints (14):
    c: Coincident(g-6,g0)
    c: Coincident(g0,g-4)
    c: Coincident(g0,g1)
    c: PointOnObject(g1,g-4)
    c: Coincident(g1,g2)
    c: Coincident(g2,g0)
    c: Coincident(g-5,g3)
    c: PointOnObject(g3,g-7)
    c: Coincident(g3,g4)
    c: Coincident(g4,g-7)
    c: Coincident(g4,g5)
    c: Coincident(g5,g3)
    c: Angle(g2,g-3) = 0.436332
    c: Equal(g3,g2)
FEATURE [PartDesign::Pocket] Pocket014004
  Length = 5
  Sketch = -> Sketch022
  Type = 1
FEATURE [Sketcher::SketchObject] Sketch023
  ExternalGeometry = -> [Pocket014004]
  Placement = pos=(-14.305,0,30.6772) rot=(0,-1,0;0.436332rad)
  Support = -> Pocket014004 [Face20]
  sketch-geometry (1):
    g0: Circle CenterX=52.4597 CenterY=-47.6154 CenterZ=0 NormalX=0 NormalY=0 NormalZ=1 Radius=1.7
  constraints (3):
    c: DistanceX(g0,g-3) = 3
    c: Radius(g0) = 1.7
    c: DistanceY(g0,g-3) = 4
FEATURE [PartDesign::Pocket] Pocket014005
  Length = 5
  Sketch = -> Sketch023
  Type = 0
FEATURE [Sketcher::SketchObject] Sketch024
  ExternalGeometry = -> [Pocket014005]
  Placement = pos=(-14.305,0,30.6772) rot=(0,-1,0;0.436332rad)
  Support = -> Pocket014005 [Face20]
  sketch-geometry (4):
    g0: LineSegment StartX=55.4597 StartY=-43.6154 StartZ=0 EndX=30.6794 EndY=-43.6154 EndZ=0
    g1: LineSegment StartX=30.6794 StartY=-43.6154 StartZ=0 EndX=30.6794 EndY=-45.6154 EndZ=0
    g2: LineSegment StartX=30.6794 StartY=-45.6154 StartZ=0 EndX=55.4597 EndY=-45.6154 EndZ=0
    g3: LineSegment StartX=55.4597 StartY=-45.6154 StartZ=0 EndX=55.4597 EndY=-43.6154 EndZ=0
  constraints (11):
    c: Coincident(g0,g1)
    c: Coincident(g1,g2)
    c: Coincident(g2,g3)
    c: Coincident(g3,g0)
    c: Horizontal(g0)
    c: Horizontal(g2)
    c: Vertical(g1)
    c: Vertical(g3)
    c: Coincident(g0,g-3)
    c: Coincident(g0,g-3)
    c: DistanceY(g3) = 2
FEATURE [PartDesign::Pad] Pad005
  Length = 1
  Length2 = 100
  Sketch = -> Sketch024
  Type = 0
FEATURE [Sketcher::SketchObject] Sketch025
  ExternalGeometry = -> [Pad005]
  Placement = pos=(8.08289,4.66666,0) rot=(0.377964,0.654654,0.654654;2.41886rad)
  Support = -> Pad005 [Face19]
  sketch-geometry (5):
    g0: LineSegment [constr] StartX=-59.7928 StartY=50 StartZ=0 EndX=-59.7928 EndY=24 EndZ=0
    g1: LineSegment [constr] StartX=-59.7928 StartY=50 StartZ=0 EndX=-55.7513 EndY=50 EndZ=0
    g2: LineSegment [constr] StartX=-59.7928 StartY=50 StartZ=0 EndX=-63.8342 EndY=50 EndZ=0
    g3: Circle CenterX=-59.7928 CenterY=50 CenterZ=0 NormalX=0 NormalY=0 NormalZ=1 Radius=2.7
    g4: Circle CenterX=-59.7928 CenterY=24 CenterZ=0 NormalX=0 NormalY=0 NormalZ=1 Radius=2.7
  constraints (14):
    c: Vertical(g0)
    c: DistanceY(g0,g-4) = 6
    c: DistanceY(g0) = -26
    c: Coincident(g1,g0)
    c: PointOnObject(g1,g-3)
    c: Horizontal(g1)
    c: Coincident(g2,g0)
    c: PointOnObject(g2,g-4)
    c: Horizontal(g2)
    c: Equal(g2,g1)
    c: Coincident(g3,g0)
    c: Coincident(g4,g0)
    c: Equal(g3,g4)
    c: Radius(g3) = 2.7
FEATURE [PartDesign::Pocket] Pocket014006
  Length = 10
  Sketch = -> Sketch025
  Type = 0
FEATURE [Sketcher::SketchObject] Sketch026
  ExternalGeometry = -> [Pocket014006]
  Placement = pos=(-8.08289,4.66666,0) rot=(-0.377964,0.654654,0.654654;3.86433rad)
  Support = -> Pocket014006 [Face1]
  sketch-geometry (5):
    g0: LineSegment [constr] StartX=59.7928 StartY=46 StartZ=0 EndX=59.7928 EndY=20 EndZ=0
    g1: LineSegment [constr] StartX=59.7928 StartY=46 StartZ=0 EndX=55.7513 EndY=46 EndZ=0
    g2: LineSegment [constr] StartX=59.7928 StartY=46 StartZ=0 EndX=63.8342 EndY=46 EndZ=0
    g3: Circle CenterX=59.7928 CenterY=46 CenterZ=0 NormalX=0 NormalY=0 NormalZ=1 Radius=2.7
    g4: Circle CenterX=59.7928 CenterY=20 CenterZ=0 NormalX=0 NormalY=0 NormalZ=1 Radius=2.7
  constraints (14):
    c: Vertical(g0)
    c: Coincident(g1,g0)
    c: PointOnObject(g1,g-3)
    c: Horizontal(g1)
    c: Coincident(g2,g0)
    c: PointOnObject(g2,g-4)
    c: Horizontal(g2)
    c: Equal(g1,g2)
    c: DistanceY(g0,g-4) = 10
    c: DistanceY(g0) = -26
    c: Coincident(g3,g0)
    c: Coincident(g4,g0)
    c: Radius(g4) = 2.7
    c: Equal(g4,g3)
FEATURE [PartDesign::Pocket] Pocket014007
  Length = 10
  Sketch = -> Sketch026
  Type = 0
FEATURE [Sketcher::SketchObject] Sketch027
  ExternalGeometry = -> [Pocket014007]
  Placement = pos=(0,-43.6154,0) rot=(0,0.707107,0.707107;3.14159rad)
  Support = -> Pocket014007 [Face7]
  sketch-geometry (4):
    g0: LineSegment StartX=-40 StartY=56 StartZ=0 EndX=40 EndY=56 EndZ=0
    g1: LineSegment StartX=40 StartY=56 StartZ=0 EndX=40 EndY=55.5 EndZ=0
    g2: LineSegment StartX=40 StartY=55.5 StartZ=0 EndX=-40 EndY=55.5 EndZ=0
    g3: LineSegment StartX=-40 StartY=55.5 StartZ=0 EndX=-40 EndY=56 EndZ=0
  constraints (11):
    c: Coincident(g0,g1)
    c: Coincident(g1,g2)
    c: Coincident(g2,g3)
    c: Coincident(g3,g0)
    c: Horizontal(g0)
    c: Horizontal(g2)
    c: Vertical(g1)
    c: Vertical(g3)
    c: Coincident(g0,g-3)
    c: Coincident(g0,g-4)
    c: DistanceY(g3) = 0.5
FEATURE [PartDesign::Pocket] Pocket014008
  Length = 5
  Sketch = -> Sketch027
  Type = 1
FEATURE [Sketcher::SketchObject] Sketch028
  Placement = pos=(0,0,55.5) rot=(0,0,1;0rad)
  Support = -> Pocket014008 [Face31]
  sketch-geometry (4):
    g0: ArcOfCircle CenterX=-5 CenterY=-5 CenterZ=0 NormalX=0 NormalY=0 NormalZ=1 Radius=37.5 StartAngle=1.5708 EndAngle=4.71239
    g1: ArcOfCircle CenterX=5 CenterY=-5 CenterZ=0 NormalX=0 NormalY=0 NormalZ=1 Radius=37.5 StartAngle=4.71239 EndAngle=7.85398
    g2: LineSegment StartX=-5 StartY=-42.5 StartZ=0 EndX=5 EndY=-42.5 EndZ=0
    g3: LineSegment StartX=-5 StartY=32.5 StartZ=0 EndX=5 EndY=32.5 EndZ=0
  constraints (10):
    c: Tangent(g0,g3) = 1.5708
    c: Tangent(g0,g2) = -1.5708
    c: Tangent(g2,g1) = -1.5708
    c: Tangent(g3,g1) = 1.5708
    c: Horizontal(g2)
    c: Equal(g0,g1)
    c: Radius(g0) = 37.5
    c: DistanceX(g0) = -5
    c: DistanceY(g0) = -5
    c: DistanceX(g-1,g1) = 5
FEATURE [PartDesign::Pocket] Pocket014009
  Length = 48
  Sketch = -> Sketch028
  Type = 0
FEATURE [Sketcher::SketchObject] Sketch029
  ExternalGeometry = -> [Pocket014009]
  Placement = pos=(0,-50.6154,0) rot=(1,0,0;1.5708rad)
  Support = -> Pocket014009 [Face8]
  sketch-geometry (12):
    g0: LineSegment StartX=22.1 StartY=14 StartZ=0 EndX=22.1 EndY=27.0423 EndZ=0
    g1: LineSegment StartX=22.1 StartY=27.0423 StartZ=0 EndX=-38.9277 EndY=55.5 EndZ=0
    g2: LineSegment StartX=-38.9277 StartY=55.5 StartZ=0 EndX=-40 EndY=55.5 EndZ=0
    g3: LineSegment StartX=-40 StartY=55.5 StartZ=0 EndX=13.5 EndY=43.6428 EndZ=0
    g4: LineSegment StartX=13.5 StartY=43.6428 StartZ=0 EndX=13.5 EndY=39 EndZ=0
    g5: LineSegment StartX=13.5 StartY=39 StartZ=0 EndX=22.1 EndY=14 EndZ=0
    g6: LineSegment StartX=28.1596 StartY=50.4787 StartZ=0 EndX=28.1596 EndY=14 EndZ=0
    g7: LineSegment StartX=28.1596 StartY=14 StartZ=0 EndX=36.7596 EndY=14 EndZ=0
    g8: LineSegment StartX=36.7596 StartY=14 StartZ=0 EndX=40 EndY=17.9686 EndZ=0
    g9: LineSegment StartX=40 StartY=17.9686 StartZ=0 EndX=40 EndY=55.5 EndZ=0
    g10: LineSegment StartX=40 StartY=55.5 StartZ=0 EndX=38.9277 EndY=55.5 EndZ=0
    g11: LineSegment StartX=38.9277 StartY=55.5 StartZ=0 EndX=28.1596 EndY=50.4787 EndZ=0
  constraints (28):
    c: PointOnObject(g0,g-9)
    c: PointOnObject(g0,g-3)
    c: Vertical(g0)
    c: Coincident(g0,g1)
    c: Coincident(g1,g-3)
    c: Coincident(g1,g2)
    c: Coincident(g2,g-4)
    c: Coincident(g2,g3)
    c: Coincident(g3,g-10)
    c: Coincident(g3,g4)
    c: Coincident(g4,g-10)
    c: Coincident(g4,g5)
    c: Coincident(g5,g0)
    c: DistanceX(g0,g4) = -8.6
    c: PointOnObject(g6,g-6)
    c: PointOnObject(g6,g-8)
    c: Vertical(g6)
    c: Coincident(g6,g7)
    c: Coincident(g7,g-8)
    c: Coincident(g7,g8)
    c: Coincident(g8,g-7)
    c: Coincident(g8,g9)
    c: Coincident(g9,g-5)
    c: Coincident(g9,g10)
    c: Coincident(g10,g-6)
    c: Coincident(g10,g11)
    c: Coincident(g11,g6)
    c: DistanceX(g6,g7) = 8.6
FEATURE [PartDesign::Pad] Pad006
  Length = 4
  Length2 = 100
  Sketch = -> Sketch029
  Type = 0
FEATURE [PartDesign::Chamfer] Chamfer007
  Base = -> Pad006 [Edge110,Edge115]
  Size = 3.9
FEATURE [PartDesign::Chamfer] Chamfer008
  Base = -> Chamfer007 [Edge170,Edge9]
  Size = 3.9
FEATURE [PartDesign::Chamfer] Chamfer009
  Base = -> Chamfer008 [Edge1,Edge115]
  Size = 3.9
FEATURE [Sketcher::SketchObject] Sketch030
  ExternalGeometry = -> [Chamfer009]
  Placement = pos=(8.08289,4.66666,0) rot=(0.377964,0.654654,0.654654;2.41886rad)
  Support = -> Chamfer009 [Face37]
  sketch-geometry (2):
    g0: Circle CenterX=-59.7928 CenterY=46 CenterZ=0 NormalX=0 NormalY=0 NormalZ=1 Radius=3.5
    g1: Circle CenterX=-59.7928 CenterY=20 CenterZ=0 NormalX=0 NormalY=0 NormalZ=1 Radius=3.5
  constraints (4):
    c: Coincident(g0,g-3)
    c: Coincident(g1,g-4)
    c: Radius(g1) = 3.5
    c: Equal(g1,g0)
FEATURE [PartDesign::Pad] Pad007
  Length = 8
  Length2 = 100
  Reversed = true
  Sketch = -> Sketch030
  Type = 0
FEATURE [Sketcher::SketchObject] Sketch031
  ExternalGeometry = -> [Pad007]
  Placement = pos=(-8.08289,4.66666,0) rot=(-0.377964,0.654654,0.654654;3.86433rad)
  Support = -> Pad007 [Face16]
  sketch-geometry (2):
    g0: Circle CenterX=59.7928 CenterY=46 CenterZ=0 NormalX=0 NormalY=0 NormalZ=1 Radius=3.5
    g1: Circle CenterX=59.7928 CenterY=20 CenterZ=0 NormalX=0 NormalY=0 NormalZ=1 Radius=3.5
  constraints (4):
    c: Coincident(g0,g-3)
    c: Coincident(g1,g-4)
    c: Radius(g1) = 3.5
    c: Equal(g1,g0)
FEATURE [PartDesign::Pad] Pad008
  Length = 8
  Length2 = 100
  Reversed = true
  Sketch = -> Sketch031
  Type = 0
FEATURE [Sketcher::SketchObject] Sketch032
  ExternalGeometry = -> [Pad008]
  Placement = pos=(-8.08289,4.66666,0) rot=(-0.377964,0.654654,0.654654;3.86433rad)
  Support = -> Pad008 [Face16]
  sketch-geometry (3):
    g0: LineSegment [constr] StartX=59.7913 StartY=49.5 StartZ=0 EndX=59.7913 EndY=24.1 EndZ=0
    g1: Circle CenterX=59.7913 CenterY=49.5 CenterZ=0 NormalX=0 NormalY=0 NormalZ=1 Radius=2.7
    g2: Circle CenterX=59.7913 CenterY=24.1 CenterZ=0 NormalX=0 NormalY=0 NormalZ=1 Radius=2.7
  constraints (8):
    c: Vertical(g0)
    c: DistanceY(g0) = -25.4
    c: DistanceX(g0,g-3) = -4.04
    c: Coincident(g1,g0)
    c: Coincident(g2,g0)
    c: Radius(g2) = 2.7
    c: Equal(g2,g1)
    c: DistanceY(g0,g-4) = 6
FEATURE [PartDesign::Pocket] Pocket014010
  Length = 6
  Sketch = -> Sketch032
  Type = 0
FEATURE [Sketcher::SketchObject] Sketch033
  ExternalGeometry = -> [Pocket014010]
  Placement = pos=(-14.305,0,30.6772) rot=(0,-1,0;0.436332rad)
  Support = -> Pocket014010 [Face23]
  sketch-geometry (1):
    g0: Circle CenterX=52.4597 CenterY=-47.6154 CenterZ=0 NormalX=0 NormalY=0 NormalZ=1 Radius=2.25
  constraints (2):
    c: Coincident(g0,g-3)
    c: Radius(g0) = 2.25
FEATURE [PartDesign::Pad] Pad009
  Length = 5
  Length2 = 100
  Reversed = true
  Sketch = -> Sketch033
  Type = 0
FEATURE [Sketcher::SketchObject] Sketch034
  ExternalGeometry = -> [Pad009]
  Placement = pos=(-14.305,0,30.6772) rot=(0,-1,0;0.436332rad)
  Support = -> Pad009 [Face23]
  sketch-geometry (2):
    g0: LineSegment [constr] StartX=52.4597 StartY=-47.6154 StartZ=0 EndX=46.4597 EndY=-47.6154 EndZ=0
    g1: Circle CenterX=46.4597 CenterY=-47.6154 CenterZ=0 NormalX=0 NormalY=0 NormalZ=1 Radius=1.7
  constraints (5):
    c: Coincident(g0,g-3)
    c: Horizontal(g0)
    c: DistanceX(g0) = -6
    c: Coincident(g1,g0)
    c: Equal(g-4,g1)
FEATURE [PartDesign::Pocket] Pocket014011
  Length = 5
  Sketch = -> Sketch034
  Type = 0
FEATURE [Sketcher::SketchObject] Sketch035
  ExternalGeometry = -> [Pocket014011]
  Placement = pos=(8.08289,4.66666,0) rot=(0.377964,0.654654,0.654654;2.41886rad)
  Support = -> Pocket014011 [Face39]
  sketch-geometry (3):
    g0: LineSegment [constr] StartX=-59.7942 StartY=49.5 StartZ=0 EndX=-59.7942 EndY=24.1 EndZ=0
    g1: Circle CenterX=-59.7942 CenterY=49.5 CenterZ=0 NormalX=0 NormalY=0 NormalZ=1 Radius=2.7
    g2: Circle CenterX=-59.7942 CenterY=24.1 CenterZ=0 NormalX=0 NormalY=0 NormalZ=1 Radius=2.7
  constraints (8):
    c: Vertical(g0)
    c: DistanceY(g0) = -25.4
    c: DistanceY(g0,g-4) = 6
    c: DistanceX(g0,g-4) = -4.04
    c: Coincident(g1,g0)
    c: Coincident(g2,g0)
    c: Radius(g1) = 2.7
    c: Equal(g1,g2)
FEATURE [PartDesign::Pocket] Pocket014012
  Length = 6
  Sketch = -> Sketch035
  Type = 0
FEATURE [Sketcher::SketchObject] Sketch036
  ExternalGeometry = -> [Pocket014012]
  Placement = pos=(0,0,6) rot=(0,0,1;0rad)
  Support = -> Pocket014012 [Face72]
  sketch-geometry (8):
    g0: LineSegment StartX=50 StartY=-24.5 StartZ=0 EndX=44 EndY=-24.5 EndZ=0
    g1: LineSegment StartX=44 StartY=-24.5 StartZ=0 EndX=44 EndY=-18.5 EndZ=0
    g2: LineSegment StartX=44 StartY=-18.5 StartZ=0 EndX=50 EndY=-18.5 EndZ=0
    g3: LineSegment StartX=50 StartY=-18.5 StartZ=0 EndX=50 EndY=-24.5 EndZ=0
    g4: LineSegment StartX=50 StartY=25.5 StartZ=0 EndX=44 EndY=25.5 EndZ=0
    g5: LineSegment StartX=44 StartY=25.5 StartZ=0 EndX=44 EndY=31.5 EndZ=0
    g6: LineSegment StartX=44 StartY=31.5 StartZ=0 EndX=50 EndY=31.5 EndZ=0
    g7: LineSegment StartX=50 StartY=31.5 StartZ=0 EndX=50 EndY=25.5 EndZ=0
  constraints (24):
    c: Coincident(g0,g1)
    c: Coincident(g1,g2)
    c: Coincident(g2,g3)
    c: Coincident(g3,g0)
    c: Horizontal(g0)
    c: Horizontal(g2)
    c: Vertical(g1)
    c: Vertical(g3)
    c: PointOnObject(g0,g-3)
    c: Coincident(g4,g5)
    c: Coincident(g5,g6)
    c: Coincident(g6,g7)
    c: Coincident(g7,g4)
    c: Horizontal(g4)
    c: Horizontal(g6)
    c: Vertical(g5)
    c: Vertical(g7)
    c: PointOnObject(g4,g-4)
    c: Equal(g4,g2)
    c: Equal(g1,g5)
    c: DistanceY(g5) = 6
    c: DistanceY(g6,g-4) = 10
    c: DistanceY(g2,g-4) = 60
    c: DistanceX(g0) = -6
FEATURE [PartDesign::Pocket] Pocket014013
  Length = 4
  Sketch = -> Sketch036
  Type = 0
FEATURE [PartDesign::Fillet] Fillet003
  Base = -> Pocket014013 [Edge372,Edge367]
  Radius = 3.9
FEATURE [Sketcher::SketchObject] Sketch037
  ExternalGeometry = -> [Fillet003]
  Placement = pos=(0,0,6) rot=(0,0,1;0rad)
  Support = -> Fillet003 [Face4]
  sketch-geometry (4):
    g0: LineSegment StartX=50 StartY=36.5 StartZ=0 EndX=47 EndY=36.5 EndZ=0
    g1: LineSegment StartX=47 StartY=36.5 StartZ=0 EndX=47 EndY=-28.5 EndZ=0
    g2: LineSegment StartX=47 StartY=-28.5 StartZ=0 EndX=50 EndY=-28.5 EndZ=0
    g3: LineSegment StartX=50 StartY=-28.5 StartZ=0 EndX=50 EndY=36.5 EndZ=0
  constraints (12):
    c: Coincident(g0,g1)
    c: Coincident(g1,g2)
    c: Coincident(g2,g3)
    c: Coincident(g3,g0)
    c: Horizontal(g0)
    c: Horizontal(g2)
    c: Vertical(g1)
    c: Vertical(g3)
    c: PointOnObject(g0,g-3)
    c: DistanceY(g3) = 65
    c: DistanceY(g0,g-3) = 5
    c: DistanceX(g0) = -3
FEATURE [PartDesign::Pad] Pad010
  Length = 3
  Length2 = 1.5
  Reversed = true
  Sketch = -> Sketch037
  Type = 4
FEATURE [PartDesign::Chamfer] Chamfer010
  Base = -> Pad010 [Edge3,Edge1]
  Size = 2.9
FEATURE [PartDesign::Chamfer] Chamfer011
  Base = -> Chamfer010 [Edge14]
  Size = 2.9
FEATURE [Sketcher::SketchObject] Sketch038
  ExternalGeometry = -> [Chamfer011]
  Placement = pos=(0,0,9) rot=(0,0,1;0rad)
  Support = -> Chamfer011 [Face12]
  sketch-geometry (4):
    g0: LineSegment StartX=50 StartY=9.5 StartZ=0 EndX=44 EndY=9.5 EndZ=0
    g1: LineSegment StartX=44 StartY=9.5 StartZ=0 EndX=44 EndY=-10.5 EndZ=0
    g2: LineSegment StartX=44 StartY=-10.5 StartZ=0 EndX=50 EndY=-10.5 EndZ=0
    g3: LineSegment StartX=50 StartY=-10.5 StartZ=0 EndX=50 EndY=9.5 EndZ=0
  constraints (12):
    c: Coincident(g0,g1)
    c: Coincident(g1,g2)
    c: Coincident(g2,g3)
    c: Coincident(g3,g0)
    c: Horizontal(g0)
    c: Horizontal(g2)
    c: Vertical(g1)
    c: Vertical(g3)
    c: PointOnObject(g0,g-4)
    c: DistanceY(g0,g-3) = 32
    c: DistanceY(g1) = -20
    c: DistanceX(g0) = -6
FEATURE [PartDesign::Pocket] Pocket014014
  Length = 3
  Sketch = -> Sketch038
  Type = 0
FEATURE [Sketcher::SketchObject] Sketch039
  ExternalGeometry = -> [Pocket014014]
  Placement = pos=(0,-54.6154,0) rot=(1,0,0;1.5708rad)
  Support = -> Pocket014014 [Face165]
  sketch-geometry (3):
    g0: LineSegment StartX=40 StartY=55.5 StartZ=0 EndX=13.5 EndY=39 EndZ=0
    g1: LineSegment StartX=13.5 StartY=39 StartZ=0 EndX=13.5 EndY=55.5 EndZ=0
    g2: LineSegment StartX=13.5 StartY=55.5 StartZ=0 EndX=40 EndY=55.5 EndZ=0
  constraints (7):
    c: Coincident(g0,g-5)
    c: Coincident(g0,g-9)
    c: Coincident(g1,g0)
    c: Vertical(g1)
    c: Coincident(g2,g1)
    c: Coincident(g2,g0)
    c: Horizontal(g2)
FEATURE [PartDesign::Pocket] Pocket014015
  Length = 6
  Sketch = -> Sketch039
  Type = 1
FEATURE [Sketcher::SketchObject] Sketch040
  ExternalGeometry = -> [Pocket014015]
  Placement = pos=(-13.7274,0,22.0471) rot=(0,-1,0;0.556902rad)
  Support = -> Pocket014015 [Face110]
  sketch-geometry (2):
    g0: Circle CenterX=49.9461 CenterY=-47.6154 CenterZ=0 NormalX=0 NormalY=0 NormalZ=1 Radius=2.3
    g1: Circle CenterX=55.2218 CenterY=-50.7512 CenterZ=0 NormalX=0 NormalY=0 NormalZ=1 Radius=3.5
  constraints (5):
    c: Coincident(g0,g-3)
    c: PointOnObject(g1,g-5)
    c: PointOnObject(g-5,g1)
    c: Radius(g1) = 3.5
    c: Radius(g0) = 2.3
FEATURE [PartDesign::Pad] Pad011
  Length = 4
  Length2 = 100
  Reversed = true
  Sketch = -> Sketch040
  Type = 0
FEATURE [Sketcher::SketchObject] Sketch041
  ExternalGeometry = -> [Pad011]
  Placement = pos=(-13.7274,0,22.0471) rot=(0,-1,0;0.556902rad)
  Support = -> Pad011 [Face110]
  sketch-geometry (2):
    g0: Circle CenterX=52.9461 CenterY=-47.6154 CenterZ=0 NormalX=0 NormalY=0 NormalZ=1 Radius=2.26954
    g1: LineSegment [constr] StartX=49.9461 StartY=-47.6154 StartZ=0 EndX=52.9461 EndY=-47.6154 EndZ=0
  constraints (4):
    c: Coincident(g1,g-3)
    c: Coincident(g1,g0)
    c: Horizontal(g1)
    c: DistanceX(g1) = 3
FEATURE [PartDesign::Pocket] Pocket014016
  Length = 7
  Sketch = -> Sketch041
  Type = 0
FEATURE [Sketcher::SketchObject] Sketch042
  ExternalGeometry = -> [Pocket014016]
  Placement = pos=(8.08289,4.66666,0) rot=(0.377964,0.654654,0.654654;2.41886rad)
  Support = -> Pocket014016 [Face105]
  sketch-geometry (1):
    g0: Circle CenterX=-59.7942 CenterY=49.5 CenterZ=0 NormalX=0 NormalY=0 NormalZ=1 Radius=2.7
  constraints (2):
    c: Coincident(g0,g-3)
    c: Equal(g0,g-3)
FEATURE [PartDesign::Pocket] Pocket014017
  Length = 3
  Sketch = -> Sketch042
  Type = 0
FEATURE [Sketcher::SketchObject] Sketch043
  ExternalGeometry = -> [Pocket014017]
  Placement = pos=(0,0,6) rot=(0,0,1;0rad)
  Support = -> Pocket014017 [Face5]
  sketch-geometry (4):
    g0: ArcOfCircle CenterX=-5 CenterY=-5 CenterZ=0 NormalX=0 NormalY=0 NormalZ=1 Radius=37.5 StartAngle=1.77215 EndAngle=3.87546
    g1: ArcOfCircle CenterX=-5 CenterY=-5 CenterZ=0 NormalX=0 NormalY=0 NormalZ=1 Radius=45 StartAngle=1.73824 EndAngle=4.04514
    g2: LineSegment StartX=-12.5 StartY=39.3706 StartZ=0 EndX=-12.5 EndY=31.7423 EndZ=0
    g3: LineSegment StartX=-32.8472 StartY=-30.1154 StartZ=0 EndX=-32.8472 EndY=-40.3487 EndZ=0
  constraints (11):
    c: Coincident(g0,g-3)
    c: Coincident(g1,g0)
    c: Coincident(g2,g1)
    c: Coincident(g2,g0)
    c: Vertical(g2)
    c: Tangent(g1,g-4)
    c: PointOnObject(g-5,g2)
    c: Coincident(g-3,g0)
    c: Coincident(g3,g0)
    c: Coincident(g3,g1)
    c: Vertical(g3)
FEATURE [PartDesign::Pad] Pad012
  Length = 6
  Length2 = 6
  Sketch = -> Sketch043
  Type = 4
FEATURE [PartDesign::Chamfer] Chamfer012
  Base = -> Pad012 [Edge48]
  Size = 5.99
FEATURE [PartDesign::Chamfer] Chamfer013
  Base = -> Chamfer012 [Edge74]
  Size = 2
FEATURE [PartDesign::Chamfer] Chamfer014
  Base = -> Chamfer013 [Edge13]
  Size = 3
FEATURE [Sketcher::SketchObject] Sketch044
  ExternalGeometry = -> [Chamfer014]
  Placement = pos=(0,0,6) rot=(0,0,1;0rad)
  Support = -> Chamfer014 [Face7]
  sketch-geometry (6):
    g0: ArcOfCircle CenterX=-0.816614 CenterY=-5.46774 CenterZ=0 NormalX=0 NormalY=0 NormalZ=1 Radius=49.2095 StartAngle=1.8738 EndAngle=3.03025
    g1: LineSegment [constr] StartX=-49.7214 StartY=1.4e-11 StartZ=0 EndX=-49.7214 EndY=41.5 EndZ=0
    g2: LineSegment StartX=-15.5 StartY=41.5 StartZ=0 EndX=-49.7214 EndY=41.5 EndZ=0
    g3: LineSegment StartX=-49.7214 StartY=1.4e-11 StartZ=0 EndX=-52.7214 EndY=1.4e-11 EndZ=0
    g4: LineSegment StartX=-52.7214 StartY=1.4e-11 StartZ=0 EndX=-52.7214 EndY=41.5 EndZ=0
    g5: LineSegment StartX=-52.7214 StartY=41.5 StartZ=0 EndX=-49.7214 EndY=41.5 EndZ=0
  constraints (17):
    c: PointOnObject(g0,g-3)
    c: Coincident(g0,g-4)
    c: Tangent(g-3,g0)
    c: PointOnObject(g0,g-1)
    c: Coincident(g2,g0)
    c: Coincident(g2,g1)
    c: Horizontal(g2)
    c: Vertical(g1)
    c: Coincident(g0,g1)
    c: Coincident(g3,g4)
    c: Vertical(g4)
    c: Coincident(g4,g5)
    c: Coincident(g5,g1)
    c: Horizontal(g5)
    c: Horizontal(g3)
    c: DistanceX(g5) = 3
    c: Coincident(g3,g0)
FEATURE [PartDesign::Pocket] Pocket014018
  Length = 5
  Sketch = -> Sketch044
  Type = 1
FEATURE [PartDesign::Chamfer] Chamfer015
  Base = -> Pocket014018 [Edge6]
  Size = 4
FEATURE [Sketcher::SketchObject] Sketch045
  ExternalGeometry = -> [Chamfer015]
  Placement = pos=(0,-43.6154,0) rot=(0,0.707107,0.707107;3.14159rad)
  Support = -> Chamfer015 [Face58]
  sketch-geometry (2):
    g0: Circle CenterX=-25 CenterY=39 CenterZ=0 NormalX=0 NormalY=0 NormalZ=1 Radius=4.125
    g1: Circle CenterX=25 CenterY=39 CenterZ=0 NormalX=0 NormalY=0 NormalZ=1 Radius=4.125
  constraints (4):
    c: Coincident(g0,g-3)
    c: Coincident(g1,g-4)
    c: Radius(g1) = 4.125
    c: Equal(g1,g0)
FEATURE [PartDesign::Pad] Pad013
  Length = 7
  Length2 = 100
  Reversed = true
  Sketch = -> Sketch045
  Type = 0
FEATURE [Sketcher::SketchObject] Sketch046
  ExternalGeometry = -> [Pad013]
  Placement = pos=(0,-43.6154,0) rot=(0,0.707107,0.707107;3.14159rad)
  Support = -> Pad013 [Face58]
  sketch-geometry (3):
    g0: Circle CenterX=-23 CenterY=39 CenterZ=0 NormalX=0 NormalY=0 NormalZ=1 Radius=2.75
    g1: Circle CenterX=27 CenterY=39 CenterZ=0 NormalX=0 NormalY=0 NormalZ=1 Radius=2.75
    g2: LineSegment [constr] StartX=-23 StartY=39 StartZ=0 EndX=27 EndY=39 EndZ=0
  constraints (8):
    c: Coincident(g2,g0)
    c: Coincident(g2,g1)
    c: Horizontal(g2)
    c: DistanceX(g2) = 50
    c: PointOnObject(g-4,g2)
    c: DistanceX(g1,g-4) = -2
    c: Equal(g0,g-3)
    c: Equal(g-3,g1)
FEATURE [PartDesign::Pocket] Pocket014019
  Length = 5
  Sketch = -> Sketch046
  Type = 1
FEATURE [PartDesign::Fillet] Fillet004
  Base = -> Pocket014019 [Edge374,Edge378]
  Radius = 6
FEATURE [Sketcher::SketchObject] Sketch047
  Placement = pos=(0,0,0) rot=(1,0,0;3.14159rad)
  Support = -> Fillet004 [Face153]
  sketch-geometry (5):
    g0: LineSegment StartX=40 StartY=35 StartZ=0 EndX=-40 EndY=35 EndZ=0
    g1: LineSegment StartX=-40 StartY=35 StartZ=0 EndX=-40 EndY=-15 EndZ=0
    g2: LineSegment StartX=40 StartY=-35 StartZ=0 EndX=40 EndY=35 EndZ=0
    g3: LineSegment StartX=-40 StartY=-15 StartZ=0 EndX=-20 EndY=-35 EndZ=0
    g4: LineSegment StartX=-20 StartY=-35 StartZ=0 EndX=40 EndY=-35 EndZ=0
  constraints (15):
    c: Coincident(g0,g1)
    c: Coincident(g2,g0)
    c: Horizontal(g0)
    c: Vertical(g1)
    c: Vertical(g2)
    c: Coincident(g1,g3)
    c: Coincident(g3,g4)
    c: Horizontal(g4)
    c: Coincident(g4,g2)
    c: DistanceX(g0) = 40
    c: DistanceY(g0) = 35
    c: Angle(g3,g1) = 2.35619
    c: DistanceX(g0) = -80
    c: DistanceY(g2) = 70
    c: DistanceX(g4) = 60
FEATURE [PartDesign::Pad] Pad014
  Length = 6
  Length2 = 100
  Reversed = true
  Sketch = -> Sketch047
  Type = 0
FEATURE [Sketcher::SketchObject] Sketch048
  Placement = pos=(0,0,7.5) rot=(0,0,1;0rad)
  Support = -> Pad014 [Face37]
  sketch-geometry (3):
    g0: ArcOfCircle CenterX=0 CenterY=0 CenterZ=0 NormalX=0 NormalY=0 NormalZ=1 Radius=27.5 StartAngle=1.5708 EndAngle=6.28319
    g1: LineSegment StartX=0 StartY=27.5 StartZ=0 EndX=27.5 EndY=27.5 EndZ=0
    g2: LineSegment StartX=27.5 StartY=27.5 StartZ=0 EndX=27.5 EndY=6.44553e-05 EndZ=0
  constraints (8):
    c: Coincident(g0,g-1)
    c: Tangent(g0,g1) = 1.5708
    c: Coincident(g1,g2)
    c: Coincident(g2,g0)
    c: Tangent(g0,g2)
    c: Horizontal(g1)
    c: Vertical(g2)
    c: DistanceY(g-1,g0) = 27.5
FEATURE [PartDesign::Pocket] Pocket014020
  Length = 4
  Sketch = -> Sketch048
  Type = 0
FEATURE [PartDesign::Fillet] Fillet005
  Base = -> Pocket014020 [Edge448,Edge451]
  Radius = 1
FEATURE [Part::Feature] Fillet005001  label="Fillet006"
  shape: bbox 100 x 117.7 x 55.5 mm, 168 faces (baked)
FEATURE [PartDesign::Fillet] Fillet005002
  Base = -> Fillet005001 [Edge50]
  Radius = 1.4
FEATURE [PartDesign::Fillet] Fillet005003
  Base = -> Fillet005002 [Edge5]
  Radius = 3
FEATURE [PartDesign::Fillet] Fillet005004
  Base = -> Fillet005003 [Edge117]
  Radius = 3
FEATURE [Sketcher::SketchObject] Sketch049
  ExternalGeometry = -> [Fillet005004]
  Placement = pos=(0,0,55.5) rot=(0,0,1;0rad)
  Support = -> Fillet005004 [Face126]
  sketch-geometry (4):
    g0: LineSegment StartX=-12.5 StartY=51.1 StartZ=0 EndX=0 EndY=51.1 EndZ=0
    g1: LineSegment StartX=0 StartY=51.1 StartZ=0 EndX=0 EndY=21.1 EndZ=0
    g2: LineSegment StartX=0 StartY=21.1 StartZ=0 EndX=-12.5 EndY=21.1 EndZ=0
    g3: LineSegment StartX=-12.5 StartY=21.1 StartZ=0 EndX=-12.5 EndY=51.1 EndZ=0
  constraints (11):
    c: Coincident(g0,g1)
    c: Coincident(g1,g2)
    c: Coincident(g2,g3)
    c: Coincident(g3,g0)
    c: Horizontal(g0)
    c: Horizontal(g2)
    c: Vertical(g1)
    c: Vertical(g3)
    c: Coincident(g0,g-3)
    c: PointOnObject(g1,g-2)
    c: DistanceY(g1) = -30
FEATURE [PartDesign::Pocket] Pocket014021
  Length = 49.5
  Sketch = -> Sketch049
  Type = 0
FEATURE [Sketcher::SketchObject] Sketch050
  ExternalGeometry = -> [Pocket014021]
  Placement = pos=(0,41.5,0) rot=(0,0.707107,0.707107;3.14159rad)
  Support = -> Pocket014021 [Face67]
  sketch-geometry (3):
    g0: LineSegment StartX=12.5 StartY=6 StartZ=0 EndX=12.5 EndY=14 EndZ=0
    g1: LineSegment StartX=12.5 StartY=14 StartZ=0 EndX=52.5 EndY=14 EndZ=0
    g2: LineSegment StartX=52.5 StartY=14 StartZ=0 EndX=12.5 EndY=6 EndZ=0
  constraints (8):
    c: Vertical(g0)
    c: Coincident(g0,g1)
    c: Horizontal(g1)
    c: Coincident(g1,g2)
    c: DistanceX(g1) = 40
    c: Coincident(g2,g0)
    c: Coincident(g-3,g0)
    c: DistanceY(g0) = 8
FEATURE [PartDesign::Pocket] Pocket014022
  Length = 40
  Sketch = -> Sketch050
  Type = 0
FEATURE [PartDesign::Chamfer] Chamfer016
  Base = -> Pocket014022 [Edge11]
  Size = 2
FEATURE [Sketcher::SketchObject] Sketch051
  ExternalGeometry = -> [Chamfer016]
  Placement = pos=(0,-50.6154,0) rot=(1,0,0;1.5708rad)
  Support = -> Chamfer016 [Face110]
  sketch-geometry (4):
    g0: LineSegment StartX=-8 StartY=20 StartZ=0 EndX=8 EndY=20 EndZ=0
    g1: LineSegment StartX=8 StartY=20 StartZ=0 EndX=8 EndY=16 EndZ=0
    g2: LineSegment StartX=8 StartY=16 StartZ=0 EndX=-8 EndY=16 EndZ=0
    g3: LineSegment StartX=-8 StartY=16 StartZ=0 EndX=-8 EndY=20 EndZ=0
  constraints (12):
    c: Coincident(g0,g1)
    c: Coincident(g1,g2)
    c: Coincident(g2,g3)
    c: Coincident(g3,g0)
    c: Horizontal(g0)
    c: Horizontal(g2)
    c: Vertical(g1)
    c: Vertical(g3)
    c: PointOnObject(g-3,g2)
    c: DistanceX(g2,g-3) = 8
    c: DistanceY(g1) = -4
    c: DistanceX(g0) = 16
FEATURE [PartDesign::Pocket] Pocket014023
  Length = 5
  Sketch = -> Sketch051
  Type = 0
FEATURE [PartDesign::Fillet] Fillet005005
  Base = -> Pocket014023 [Edge518,Edge515]
  Radius = 4.9
FEATURE [Sketcher::SketchObject] Sketch052
  ExternalGeometry = -> [Fillet005005]
  Placement = pos=(0,-50.6154,0) rot=(1,0,0;1.5708rad)
  Support = -> Fillet005005 [Face4]
  sketch-geometry (4):
    g0: LineSegment StartX=-3.09485 StartY=20 StartZ=0 EndX=3.20515 EndY=20 EndZ=0
    g1: LineSegment StartX=3.20515 StartY=20 StartZ=0 EndX=3.20515 EndY=16 EndZ=0
    g2: LineSegment StartX=3.20515 StartY=16 StartZ=0 EndX=-3.09485 EndY=16 EndZ=0
    g3: LineSegment StartX=-3.09485 StartY=16 StartZ=0 EndX=-3.09485 EndY=20 EndZ=0
  constraints (12):
    c: Coincident(g0,g1)
    c: Coincident(g1,g2)
    c: Coincident(g2,g3)
    c: Coincident(g3,g0)
    c: Horizontal(g0)
    c: Horizontal(g2)
    c: Vertical(g1)
    c: Vertical(g3)
    c: PointOnObject(g0,g-3)
    c: PointOnObject(g1,g-4)
    c: DistanceX(g1,g-4) = -3
    c: DistanceX(g0,g0) = 6.3
FEATURE [PartDesign::Pad] Pad015
  Length = 2
  Length2 = 100
  Reversed = true
  Sketch = -> Sketch052
  Type = 0
FEATURE [Sketcher::SketchObject] Sketch053
  ExternalGeometry = -> [Pad015]
  Placement = pos=(0,0,6) rot=(0,0,1;0rad)
  Support = -> Pad015 [Face50]
  sketch-geometry (1):
    g0: Circle CenterX=43.3668 CenterY=-0.5 CenterZ=0 NormalX=0 NormalY=0 NormalZ=1 Radius=12
  constraints (3):
    c: PointOnObject(g-4,g0)
    c: PointOnObject(g-3,g0)
    c: Radius(g0) = 12
FEATURE [PartDesign::Pad] Pad016
  Length = 6
  Length2 = 100
  Reversed = true
  Sketch = -> Sketch053
  Type = 0
FEATURE [Sketcher::SketchObject] Sketch054
  ExternalGeometry = -> [Pad016]
  Placement = pos=(0,0,9) rot=(0,0,1;0rad)
  Support = -> Pad016 [Face148]
  sketch-geometry (4):
    g0: ArcOfCircle CenterX=43.3668 CenterY=-0.5 CenterZ=0 NormalX=0 NormalY=0 NormalZ=1 Radius=12 StartAngle=5.29807 EndAngle=7.2683
    g1: ArcOfCircle CenterX=41.3668 CenterY=-0.5 CenterZ=0 NormalX=0 NormalY=0 NormalZ=1 Radius=11.4775 StartAngle=5.2254 EndAngle=7.34097
    g2: LineSegment StartX=47 StartY=9.5 StartZ=0 EndX=50 EndY=9.5 EndZ=0
    g3: LineSegment StartX=47 StartY=-10.5 StartZ=0 EndX=50 EndY=-10.5 EndZ=0
  constraints (10):
    c: Coincident(g0,g-3)
    c: Coincident(g0,g-4)
    c: Coincident(g1,g-3)
    c: Coincident(g1,g-4)
    c: Radius(g0) = 12
    c: DistanceX(g1,g0) = 2
    c: Coincident(g2,g1)
    c: Coincident(g2,g0)
    c: Coincident(g3,g1)
    c: Coincident(g3,g0)
FEATURE [PartDesign::Pad] Pad017
  Length = 4
  Length2 = 6
  Reversed = true
  Sketch = -> Sketch054
  Type = 4
FEATURE [PartDesign::Fillet] Fillet005006
  Base = -> Pad017 [Edge458,Edge394]
  Radius = 6
FEATURE [PartDesign::Chamfer] Chamfer017
  Base = -> Pad017 [Edge582,Edge581]
  Size = 2
FEATURE [PartDesign::Chamfer] Chamfer018
  Base = -> Chamfer017 [Edge11,Edge35]
  Size = 1.9
FEATURE [Part::Feature] Chamfer018001  label="Chamfer019"
  shape: bbox 107.3 x 117.7 x 55.51 mm, 198 faces (baked)
FEATURE [Sketcher::SketchObject] Sketch055
  ExternalGeometry = -> [Chamfer018001]
  Placement = pos=(0,0,6) rot=(0,0,1;0rad)
  Support = -> Chamfer018001 [Face149]
  sketch-geometry (1):
    g0: Circle CenterX=41.3668 CenterY=-0.5 CenterZ=0 NormalX=0 NormalY=0 NormalZ=1 Radius=6
  constraints (2):
    c: Coincident(g0,g-3)
    c: Radius(g0) = 6
FEATURE [PartDesign::Pocket] Pocket014024
  Length = 5
  Sketch = -> Sketch055
  Type = 1
FEATURE [PartDesign::Fillet] Fillet005007
  Base = -> Pocket014024 [Edge188,Edge221]
  Radius = 3
FEATURE [PartDesign::Fillet] Fillet005008
  Base = -> Fillet005007 [Edge69]
  Radius = 1
FEATURE [PartDesign::Fillet] Fillet005009
  Base = -> Fillet005008 [Edge245]
  Radius = 1
FEATURE [Sketcher::SketchObject] Sketch056
  ExternalGeometry = -> [Fillet005009]
  Placement = pos=(0,-54.6154,0) rot=(1,0,0;1.5708rad)
  Support = -> Fillet005009 [Face177]
  sketch-geometry (1):
    g0: Circle CenterX=-27 CenterY=39 CenterZ=0 NormalX=0 NormalY=0 NormalZ=1 Radius=5
  constraints (2):
    c: Coincident(g0,g-4)
    c: Radius(g0) = 5
FEATURE [PartDesign::Pocket] Pocket014025
  Length = 4
  Sketch = -> Sketch056
  Type = 0
FEATURE [Part::Feature] Pocket014025001  label="Pocket014026"
  shape: bbox 107.6 x 117.7 x 55.51 mm, 206 faces (baked)
FEATURE [Sketcher::SketchObject] Sketch057
  ExternalGeometry = -> [Pocket014025001]
  Placement = pos=(0,0,13) rot=(0,0,1;0rad)
  Support = -> Pocket014025001 [Face14]
  sketch-geometry (1):
    g0: Circle CenterX=41.3668 CenterY=-0.5 CenterZ=0 NormalX=0 NormalY=0 NormalZ=1 Radius=12.5
  constraints (2):
    c: Coincident(g0,g-3)
    c: Radius(g0) = 12.5
FEATURE [PartDesign::Pocket] Pocket014025002
  Length = 7
  Sketch = -> Sketch057
  Type = 0
FEATURE [Sketcher::SketchObject] Sketch058
  ExternalGeometry = -> [Pocket014025002]
  Placement = pos=(-13.7274,0,22.0471) rot=(0,-1,0;0.556902rad)
  Support = -> Pocket014025002 [Face103]
  sketch-geometry (1):
    g0: Circle CenterX=52.9461 CenterY=-47.6154 CenterZ=0 NormalX=0 NormalY=0 NormalZ=1 Radius=3
  constraints (2):
    c: Coincident(g0,g-3)
    c: Radius(g0) = 3
FEATURE [PartDesign::Pad] Pad018
  Length = 5
  Length2 = 100
  Reversed = true
  Sketch = -> Sketch058
  Type = 0
FEATURE [Sketcher::SketchObject] Sketch059
  ExternalGeometry = -> [Pad018]
  Placement = pos=(8.08289,4.66666,0) rot=(0.377964,0.654654,0.654654;2.41886rad)
  Support = -> Pad018 [Face64]
  sketch-geometry (1):
    g0: Circle CenterX=-59.7942 CenterY=49.5 CenterZ=0 NormalX=0 NormalY=0 NormalZ=1 Radius=2.7
  constraints (2):
    c: Coincident(g0,g-3)
    c: PointOnObject(g-3,g0)
FEATURE [PartDesign::Pocket] Pocket014025003
  Length = 5
  Sketch = -> Sketch059
  Type = 0
FEATURE [Sketcher::SketchObject] Sketch060
  ExternalGeometry = -> [Pocket014025003]
  Placement = pos=(0,-43.6154,0) rot=(0,0.707107,0.707107;3.14159rad)
  Support = -> Pocket014025003 [Face104]
  sketch-geometry (4):
    g0: LineSegment StartX=-40 StartY=55.5 StartZ=0 EndX=40 EndY=55.5 EndZ=0
    g1: LineSegment StartX=40 StartY=55.5 StartZ=0 EndX=40 EndY=39 EndZ=0
    g2: LineSegment StartX=40 StartY=39 StartZ=0 EndX=-40 EndY=39 EndZ=0
    g3: LineSegment StartX=-40 StartY=39 StartZ=0 EndX=-40 EndY=55.5 EndZ=0
  constraints (11):
    c: Coincident(g0,g1)
    c: Coincident(g1,g2)
    c: Coincident(g2,g3)
    c: Coincident(g3,g0)
    c: Horizontal(g0)
    c: Horizontal(g2)
    c: Vertical(g1)
    c: Vertical(g3)
    c: Coincident(g0,g-3)
    c: DistanceX(g0) = 80
    c: PointOnObject(g-5,g2)
FEATURE [PartDesign::Pad] Pad019
  Length = 7
  Length2 = 100
  Reversed = true
  Sketch = -> Sketch060
  Type = 0
FEATURE [Sketcher::SketchObject] Sketch061
  ExternalGeometry = -> [Pad019]
  Placement = pos=(0,0,55.5) rot=(0,0,1;0rad)
  Support = -> Pad019 [Face178]
  sketch-geometry (11):
    g0: LineSegment StartX=-40 StartY=-43.6154 StartZ=0 EndX=-40 EndY=-50.6154 EndZ=0
    g1: LineSegment StartX=-40 StartY=-50.6154 StartZ=0 EndX=-36 EndY=-54.6154 EndZ=0
    g2: LineSegment StartX=-36 StartY=-54.6154 StartZ=0 EndX=-32.0596 EndY=-54.6154 EndZ=0
    g3: LineSegment StartX=-32.0596 StartY=-54.6154 StartZ=0 EndX=-21.0596 EndY=-43.6154 EndZ=0
    g4: LineSegment StartX=-21.0596 StartY=-43.6154 StartZ=0 EndX=-40 EndY=-43.6154 EndZ=0
    g5: LineSegment StartX=28 StartY=-43.6154 StartZ=0 EndX=28 EndY=-50.6154 EndZ=0
    g6: LineSegment StartX=28 StartY=-50.6154 StartZ=0 EndX=32 EndY=-54.6154 EndZ=0
    g7: LineSegment StartX=32 StartY=-54.6154 StartZ=0 EndX=36 EndY=-54.6154 EndZ=0
    g8: LineSegment StartX=36 StartY=-54.6154 StartZ=0 EndX=40 EndY=-50.6154 EndZ=0
    g9: LineSegment StartX=40 StartY=-50.6154 StartZ=0 EndX=40 EndY=-43.6154 EndZ=0
    g10: LineSegment StartX=40 StartY=-43.6154 StartZ=0 EndX=28 EndY=-43.6154 EndZ=0
  constraints (28):
    c: Coincident(g-3,g0)
    c: Coincident(g0,g-3)
    c: Coincident(g0,g1)
    c: Coincident(g2,g1)
    c: Coincident(g2,g-4)
    c: Horizontal(g2)
    c: Coincident(g3,g2)
    c: Coincident(g4,g3)
    c: Coincident(g4,g0)
    c: Angle(g1,g-3) = 2.35619
    c: Angle(g3,g-4) = 2.35619
    c: Angle(g4,g3) = 0.785398
    c: PointOnObject(g5,g-5)
    c: Vertical(g5)
    c: Coincident(g5,g6)
    c: Coincident(g6,g7)
    c: Horizontal(g7)
    c: Coincident(g7,g8)
    c: Coincident(g8,g-6)
    c: Coincident(g8,g9)
    c: Coincident(g9,g-6)
    c: Coincident(g9,g10)
    c: Coincident(g10,g5)
    c: Angle(g6,g5) = 2.35619
    c: Angle(g-6,g8) = 2.35619
    c: DistanceX(g7) = 4
    c: DistanceY(g7,g8) = 4
    c: Equal(g5,g-6)
FEATURE [PartDesign::Pad] Pad020
  Length = 10
  Length2 = 100
  Reversed = true
  Sketch = -> Sketch061
  Type = 0
FEATURE [Sketcher::SketchObject] Sketch062
  ExternalGeometry = -> [Pad020]
  Placement = pos=(0,0,55.5) rot=(0,0,1;0rad)
  Support = -> Pad020 [Face203]
  sketch-geometry (6):
    g0: LineSegment StartX=40 StartY=-50.6154 StartZ=0 EndX=35.9585 EndY=-43.6154 EndZ=0
    g1: LineSegment StartX=35.9585 StartY=-43.6154 StartZ=0 EndX=40 EndY=-43.6154 EndZ=0
    g2: LineSegment StartX=40 StartY=-43.6154 StartZ=0 EndX=40 EndY=-50.6154 EndZ=0
    g3: LineSegment StartX=-40 StartY=-50.6154 StartZ=0 EndX=-40 EndY=-43.6154 EndZ=0
    g4: LineSegment StartX=-40 StartY=-43.6154 StartZ=0 EndX=-35.9585 EndY=-43.6154 EndZ=0
    g5: LineSegment StartX=-35.9585 StartY=-43.6154 StartZ=0 EndX=-40 EndY=-50.6154 EndZ=0
  constraints (14):
    c: Coincident(g-5,g0)
    c: PointOnObject(g0,g-6)
    c: Coincident(g0,g1)
    c: Coincident(g1,g-6)
    c: Coincident(g1,g2)
    c: Coincident(g2,g0)
    c: Coincident(g-3,g3)
    c: Coincident(g3,g-4)
    c: Coincident(g3,g4)
    c: PointOnObject(g4,g-4)
    c: Coincident(g4,g5)
    c: Coincident(g5,g3)
    c: Angle(g-5,g0) = 0.523599
    c: Angle(g5,g-3) = 0.523599
FEATURE [PartDesign::Pocket] Pocket014025004
  Length = 20
  Sketch = -> Sketch062
  Type = 0
FEATURE [Sketcher::SketchObject] Sketch063
  ExternalGeometry = -> [Pocket014025004]
  Placement = pos=(0,-43.6154,0) rot=(0,0.707107,0.707107;3.14159rad)
  Support = -> Pocket014025004 [Face167]
  sketch-geometry (1):
    g0: Circle CenterX=0 CenterY=39 CenterZ=0 NormalX=0 NormalY=0 NormalZ=1 Radius=16
  constraints (2):
    c: Coincident(g0,g-3)
    c: Radius(g0) = 16
FEATURE [PartDesign::Pad] Pad021
  Length = 7
  Length2 = 100
  Reversed = true
  Sketch = -> Sketch063
  Type = 0
FEATURE [Sketcher::SketchObject] Sketch064
  ExternalGeometry = -> [Pad021]
  Placement = pos=(0,-43.6154,0) rot=(0,0.707107,0.707107;3.14159rad)
  Support = -> Pad021 [Face103]
  sketch-geometry (8):
    g0: ArcOfCircle CenterX=2 CenterY=55.5 CenterZ=0 NormalX=0 NormalY=0 NormalZ=1 Radius=15 StartAngle=0 EndAngle=3.14159
    g1: ArcOfCircle CenterX=2 CenterY=40.5 CenterZ=0 NormalX=0 NormalY=0 NormalZ=1 Radius=15 StartAngle=3.14159 EndAngle=6.28319
    g2: LineSegment StartX=-13 StartY=55.5 StartZ=0 EndX=-13 EndY=40.5 EndZ=0
    g3: LineSegment StartX=17 StartY=55.5 StartZ=0 EndX=17 EndY=40.5 EndZ=0
    g4: LineSegment [constr] StartX=-23 StartY=39 StartZ=0 EndX=2 EndY=40.5 EndZ=0
    g5: LineSegment [constr] StartX=2 StartY=40.5 StartZ=0 EndX=27 EndY=39 EndZ=0
    g6: Circle CenterX=-23 CenterY=39 CenterZ=0 NormalX=0 NormalY=0 NormalZ=1 Radius=2.75
    g7: Circle CenterX=27 CenterY=39 CenterZ=0 NormalX=0 NormalY=0 NormalZ=1 Radius=2.75
  constraints (18):
    c: Tangent(g0,g3) = 1.5708
    c: Tangent(g0,g2) = -1.5708
    c: Tangent(g2,g1) = -1.5708
    c: Tangent(g3,g1) = 1.5708
    c: Vertical(g2)
    c: Equal(g0,g1)
    c: PointOnObject(g0,g-3)
    c: Radius(g1) = 15
    c: DistanceY(g1,g0) = 15
    c: Coincident(g4,g-4)
    c: Coincident(g4,g1)
    c: Coincident(g4,g5)
    c: Coincident(g5,g-6)
    c: Equal(g5,g4)
    c: Coincident(g6,g4)
    c: PointOnObject(g-4,g6)
    c: Coincident(g7,g5)
    c: PointOnObject(g-6,g7)
FEATURE [PartDesign::Pocket] Pocket014025005
  Length = 5
  Sketch = -> Sketch064
  Type = 1
FEATURE [Part::Feature] Pocket014025005001  label="Pocket014025006"
  shape: bbox 107.3 x 117.7 x 55.51 mm, 186 faces (baked)
FEATURE [PartDesign::Fillet] Fillet005010
  Base = -> Pocket014025005001 [Edge18,Edge15]
  Radius = 10
FEATURE [Sketcher::SketchObject] Sketch065
  ExternalGeometry = -> [Fillet005010]
  Placement = pos=(-8.08289,4.66666,0) rot=(-0.377964,0.654654,0.654654;3.86433rad)
  Support = -> Fillet005010 [Face11]
  sketch-geometry (2):
    g0: LineSegment [constr] StartX=59.7913 StartY=24.1 StartZ=0 EndX=59.7913 EndY=50.1 EndZ=0
    g1: Circle CenterX=59.7913 CenterY=50.1 CenterZ=0 NormalX=0 NormalY=0 NormalZ=1 Radius=2.7
  constraints (5):
    c: Coincident(g0,g-3)
    c: Vertical(g0)
    c: Coincident(g1,g0)
    c: Equal(g1,g-3)
    c: DistanceY(g0) = 26
FEATURE [PartDesign::Pocket] Pocket014025005002
  Length = 8
  Sketch = -> Sketch065
  Type = 0
FEATURE [Sketcher::SketchObject] Sketch066
  ExternalGeometry = -> [Pocket014025005002]
  Placement = pos=(8.08289,4.66666,0) rot=(0.377964,0.654654,0.654654;2.41886rad)
  Support = -> Pocket014025005002 [Face9]
  sketch-geometry (2):
    g0: LineSegment [constr] StartX=-59.7942 StartY=24.1 StartZ=0 EndX=-59.7942 EndY=50.1 EndZ=0
    g1: Circle CenterX=-59.7942 CenterY=50.1 CenterZ=0 NormalX=0 NormalY=0 NormalZ=1 Radius=2.7
  constraints (5):
    c: Coincident(g0,g-3)
    c: Vertical(g0)
    c: DistanceY(g0) = 26
    c: Coincident(g1,g0)
    c: Equal(g1,g-3)
FEATURE [PartDesign::Pocket] Pocket014025005003
  Length = 8
  Sketch = -> Sketch066
  Type = 0
FEATURE [Sketcher::SketchObject] Sketch067
  ExternalGeometry = -> [Pocket014025005003]
  Placement = pos=(0,0,0) rot=(1,0,0;3.14159rad)
  Support = -> Pocket014025005003 [Face162]
  sketch-geometry (4):
    g0: Circle CenterX=-49.49 CenterY=47.49 CenterZ=0 NormalX=0 NormalY=0 NormalZ=1 Radius=5.99
    g1: Circle CenterX=49.49 CenterY=47.49 CenterZ=0 NormalX=0 NormalY=0 NormalZ=1 Radius=5.99
    g2: LineSegment [constr] StartX=-49.99 StartY=47.49 StartZ=0 EndX=-49.49 EndY=47.49 EndZ=0
    g3: LineSegment [constr] StartX=49.99 StartY=47.49 StartZ=0 EndX=49.49 EndY=47.49 EndZ=0
  constraints (11):
    c: Radius(g-6) = 5.99
    c: Coincident(g2,g-6)
    c: Coincident(g2,g0)
    c: Coincident(g3,g-5)
    c: Coincident(g3,g1)
    c: Horizontal(g3)
    c: Horizontal(g2)
    c: Equal(g-6,g0)
    c: Equal(g0,g1)
    c: DistanceX(g2) = 0.5
    c: Equal(g3,g2)
FEATURE [PartDesign::Pocket] Pocket014025005004
  Length = 5
  Sketch = -> Sketch067
  Type = 1
FEATURE [Sketcher::SketchObject] Sketch068
  ExternalGeometry = -> [Pocket014025005004]
  Placement = pos=(0,0,0) rot=(1,0,0;3.14159rad)
  Support = -> Pocket014025005004 [Face163]
  sketch-geometry (8):
    g0: LineSegment StartX=-43.5 StartY=47.49 StartZ=0 EndX=-46.5 EndY=47.49 EndZ=0
    g1: LineSegment StartX=-46.5 StartY=47.49 StartZ=0 EndX=-46.5 EndY=57.49 EndZ=0
    g2: LineSegment StartX=-46.5 StartY=57.49 StartZ=0 EndX=-43.5 EndY=57.49 EndZ=0
    g3: LineSegment StartX=-43.5 StartY=57.49 StartZ=0 EndX=-43.5 EndY=47.49 EndZ=0
    g4: LineSegment StartX=43.5 StartY=47.49 StartZ=0 EndX=46.5 EndY=47.49 EndZ=0
    g5: LineSegment StartX=46.5 StartY=47.49 StartZ=0 EndX=46.5 EndY=57.49 EndZ=0
    g6: LineSegment StartX=46.5 StartY=57.49 StartZ=0 EndX=43.5 EndY=57.49 EndZ=0
    g7: LineSegment StartX=43.5 StartY=57.49 StartZ=0 EndX=43.5 EndY=47.49 EndZ=0
  constraints (23):
    c: Coincident(g0,g1)
    c: Coincident(g1,g2)
    c: Coincident(g2,g3)
    c: Coincident(g3,g0)
    c: Horizontal(g0)
    c: Horizontal(g2)
    c: Vertical(g1)
    c: Vertical(g3)
    c: Coincident(g0,g-3)
    c: Coincident(g4,g5)
    c: Coincident(g5,g6)
    c: Coincident(g6,g7)
    c: Coincident(g7,g4)
    c: Horizontal(g4)
    c: Horizontal(g6)
    c: Vertical(g5)
    c: Vertical(g7)
    c: PointOnObject(g4,g-4)
    c: Tangent(g-4,g7)
    c: Equal(g7,g3)
    c: Equal(g6,g2)
    c: DistanceY(g1) = 10
    c: DistanceX(g2) = 3
FEATURE [PartDesign::Pocket] Pocket014025005005
  Length = 5
  Sketch = -> Sketch068
  Type = 1
FEATURE [Sketcher::SketchObject] Sketch069
  ExternalGeometry = -> [Pocket014025005005]
  Placement = pos=(0,0,55.5) rot=(0,0,1;0rad)
  Support = -> Pocket014025005005 [Face8]
  sketch-geometry (4):
    g0: LineSegment StartX=43 StartY=-28.6154 StartZ=0 EndX=63 EndY=-28.6154 EndZ=0
    g1: LineSegment StartX=63 StartY=-28.6154 StartZ=0 EndX=63 EndY=46.3846 EndZ=0
    g2: LineSegment StartX=63 StartY=46.3846 StartZ=0 EndX=43 EndY=46.3846 EndZ=0
    g3: LineSegment StartX=43 StartY=46.3846 StartZ=0 EndX=43 EndY=-28.6154 EndZ=0
  constraints (11):
    c: Coincident(g0,g1)
    c: Coincident(g1,g2)
    c: Coincident(g2,g3)
    c: Coincident(g3,g0)
    c: Horizontal(g0)
    c: Horizontal(g2)
    c: Vertical(g1)
    c: Vertical(g3)
    c: Coincident(g0,g-3)
    c: DistanceY(g3) = -75
    c: DistanceX(g2) = -20
FEATURE [PartDesign::Pocket] Pocket014025005006
  Length = 0
  Sketch = -> Sketch069
  Type = 3
  UpToFace = -> Pocket014025005005 [Face38]
FEATURE [Sketcher::SketchObject] Sketch070
  ExternalGeometry = -> [Pocket014025005006]
  Placement = pos=(0,0,6) rot=(0,0,1;0rad)
  Support = -> Pocket014025005006 [Face131]
  sketch-geometry (4):
    g0: LineSegment StartX=50 StartY=-11.9978 StartZ=0 EndX=60 EndY=-11.9978 EndZ=0
    g1: LineSegment StartX=60 StartY=-11.9978 StartZ=0 EndX=60 EndY=13.0022 EndZ=0
    g2: LineSegment StartX=60 StartY=13.0022 StartZ=0 EndX=50 EndY=13.0022 EndZ=0
    g3: LineSegment StartX=50 StartY=13.0022 StartZ=0 EndX=50 EndY=-11.9978 EndZ=0
  constraints (11):
    c: Coincident(g0,g1)
    c: Coincident(g1,g2)
    c: Coincident(g2,g3)
    c: Coincident(g3,g0)
    c: Horizontal(g0)
    c: Horizontal(g2)
    c: Vertical(g1)
    c: Vertical(g3)
    c: Coincident(g0,g-3)
    c: DistanceY(g3) = -25
    c: DistanceX(g2) = -10
FEATURE [PartDesign::Pocket] Pocket014025005007
  Length = 5
  Sketch = -> Sketch070
  Type = 1
FEATURE [Sketcher::SketchObject] Sketch071
  ExternalGeometry = -> [Pocket014025005007]
  Placement = pos=(0,0,6) rot=(0,0,1;0rad)
  Support = -> Pocket014025005007 [Face48]
  sketch-geometry (8):
    g0: LineSegment StartX=50 StartY=41.5 StartZ=0 EndX=40 EndY=41.5 EndZ=0
    g1: LineSegment StartX=40 StartY=41.5 StartZ=0 EndX=40 EndY=21.5 EndZ=0
    g2: LineSegment StartX=40 StartY=21.5 StartZ=0 EndX=50 EndY=21.5 EndZ=0
    g3: LineSegment StartX=50 StartY=21.5 StartZ=0 EndX=50 EndY=41.5 EndZ=0
    g4: LineSegment StartX=50 StartY=-28.6154 StartZ=0 EndX=40 EndY=-28.6154 EndZ=0
    g5: LineSegment StartX=40 StartY=-28.6154 StartZ=0 EndX=40 EndY=-8.61539 EndZ=0
    g6: LineSegment StartX=40 StartY=-8.61539 StartZ=0 EndX=50 EndY=-8.61539 EndZ=0
    g7: LineSegment StartX=50 StartY=-8.61539 StartZ=0 EndX=50 EndY=-28.6154 EndZ=0
  constraints (22):
    c: Coincident(g0,g1)
    c: Coincident(g1,g2)
    c: Coincident(g2,g3)
    c: Coincident(g3,g0)
    c: Horizontal(g0)
    c: Horizontal(g2)
    c: Vertical(g1)
    c: Vertical(g3)
    c: Coincident(g0,g-3)
    c: Coincident(g4,g5)
    c: Coincident(g5,g6)
    c: Coincident(g6,g7)
    c: Coincident(g7,g4)
    c: Horizontal(g4)
    c: Horizontal(g6)
    c: Vertical(g5)
    c: Vertical(g7)
    c: Coincident(g4,g-4)
    c: Equal(g6,g2)
    c: Equal(g3,g7)
    c: DistanceY(g3) = 20
    c: DistanceX(g2) = 10
FEATURE [PartDesign::Pad] Pad022
  Length = 6
  Length2 = 100
  Reversed = true
  Sketch = -> Sketch071
  Type = 0
FEATURE [Sketcher::SketchObject] Sketch072
  ExternalGeometry = -> [Pad022]
  Placement = pos=(0,0,55.5) rot=(0,0,1;0rad)
  Support = -> Pad022 [Face8]
  sketch-geometry (4):
    g0: LineSegment StartX=29 StartY=-48.6154 StartZ=0 EndX=19 EndY=-48.6154 EndZ=0
    g1: LineSegment StartX=19 StartY=-48.6154 StartZ=0 EndX=19 EndY=-45.6154 EndZ=0
    g2: LineSegment StartX=19 StartY=-45.6154 StartZ=0 EndX=29 EndY=-45.6154 EndZ=0
    g3: LineSegment StartX=29 StartY=-45.6154 StartZ=0 EndX=29 EndY=-48.6154 EndZ=0
  constraints (12):
    c: Coincident(g0,g1)
    c: Coincident(g1,g2)
    c: Coincident(g2,g3)
    c: Coincident(g3,g0)
    c: Horizontal(g0)
    c: Horizontal(g2)
    c: Vertical(g1)
    c: Vertical(g3)
    c: DistanceY(g3) = -3
    c: DistanceY(g0,g-3) = -2
    c: DistanceX(g2) = 10
    c: DistanceX(g1,g-3) = 4
FEATURE [PartDesign::Pocket] Pocket014025005008
  Length = 6
  Sketch = -> Sketch072
  Type = 0
FEATURE [Sketcher::SketchObject] Sketch073
  ExternalGeometry = -> [Pocket014025005008]
  Placement = pos=(0,0,55.5) rot=(0,0,1;0rad)
  Support = -> Pocket014025005008 [Face8]
  sketch-geometry (4):
    g0: LineSegment StartX=23 StartY=-45.6154 StartZ=0 EndX=25 EndY=-45.6154 EndZ=0
    g1: LineSegment StartX=25 StartY=-45.6154 StartZ=0 EndX=25 EndY=-48.6154 EndZ=0
    g2: LineSegment StartX=25 StartY=-48.6154 StartZ=0 EndX=23 EndY=-48.6154 EndZ=0
    g3: LineSegment StartX=23 StartY=-48.6154 StartZ=0 EndX=23 EndY=-45.6154 EndZ=0
  constraints (11):
    c: Coincident(g0,g1)
    c: Coincident(g1,g2)
    c: Coincident(g2,g3)
    c: Coincident(g3,g0)
    c: Horizontal(g0)
    c: Horizontal(g2)
    c: Vertical(g1)
    c: Vertical(g3)
    c: Coincident(g0,g-3)
    c: PointOnObject(g1,g-4)
    c: DistanceX(g0) = 2
FEATURE [PartDesign::Pad] Pad023
  Length = 3
  Length2 = 100
  Reversed = true
  Sketch = -> Sketch073
  Type = 0
FEATURE [PartDesign::Fillet] Fillet005011
  Base = -> Pad023 [Edge338,Edge339]
  Radius = 0.75
FEATURE [PartDesign::Fillet] Fillet005012
  Base = -> Fillet005011 [Edge30,Edge25]
  Radius = 3
FEATURE [Part::Feature] Fillet005012001  label="Fillet005013"
  shape: bbox 101.9 x 117.7 x 55.51 mm, 176 faces (baked)
FEATURE [Sketcher::SketchObject] Sketch074
  ExternalGeometry = -> [Fillet005012001]
  Placement = pos=(0,0,6) rot=(0,0,1;0rad)
  Support = -> Fillet005012001 [Face138]
  sketch-geometry (3):
    g0: ArcOfCircle CenterX=15 CenterY=6.5 CenterZ=0 NormalX=0 NormalY=0 NormalZ=1 Radius=35 StartAngle=9.28518e-07 EndAngle=1.5708
    g1: LineSegment StartX=15 StartY=41.5 StartZ=0 EndX=50 EndY=41.5 EndZ=0
    g2: LineSegment StartX=50 StartY=41.5 StartZ=0 EndX=50 EndY=6.50003 EndZ=0
  constraints (10):
    c: PointOnObject(g0,g-3)
    c: PointOnObject(g0,g-4)
    c: Tangent(g0,g-4)
    c: Tangent(g0,g-3)
    c: Radius(g0) = 35
    c: Coincident(g1,g2)
    c: Horizontal(g1)
    c: Vertical(g2)
    c: Coincident(g1,g0)
    c: Coincident(g2,g0)
FEATURE [PartDesign::Pocket] Pocket014025005009
  Length = 5
  Sketch = -> Sketch074
  Type = 1
FEATURE [Sketcher::SketchObject] Sketch075
  Placement = pos=(0,0,55.5) rot=(0,0,1;0rad)
  Support = -> Pocket014025005009 [Face69]
  sketch-geometry (5):
    g0: Circle CenterX=23 CenterY=-50 CenterZ=0 NormalX=0 NormalY=0 NormalZ=1 Radius=2.75
    g1: LineSegment StartX=32 StartY=-44 StartZ=0 EndX=17 EndY=-44 EndZ=0
    g2: LineSegment StartX=17 StartY=-44 StartZ=0 EndX=17 EndY=-54.5 EndZ=0
    g3: LineSegment StartX=17 StartY=-54.5 StartZ=0 EndX=32 EndY=-54.5 EndZ=0
    g4: LineSegment StartX=32 StartY=-54.5 StartZ=0 EndX=32 EndY=-44 EndZ=0
  constraints (15):
    c: Radius(g0) = 2.75
    c: DistanceX(g0) = 23
    c: DistanceY(g0) = -50
    c: Coincident(g1,g2)
    c: Coincident(g2,g3)
    c: Coincident(g3,g4)
    c: Coincident(g4,g1)
    c: Horizontal(g1)
    c: Horizontal(g3)
    c: Vertical(g2)
    c: Vertical(g4)
    c: DistanceX(g1) = 32
    c: DistanceY(g1) = -44
    c: DistanceY(g4) = 10.5
    c: DistanceX(g3) = 15
FEATURE [PartDesign::Pad] Pad024
  Length = 12
  Length2 = 100
  Reversed = true
  Sketch = -> Sketch075
  Type = 0
FEATURE [Sketcher::SketchObject] Sketch076
  ExternalGeometry = -> [Pad024]
  Placement = pos=(0,0,55.5) rot=(0,0,1;0rad)
  Support = -> Pad024 [Face113]
  sketch-geometry (1):
    g0: Circle CenterX=23 CenterY=-50 CenterZ=0 NormalX=0 NormalY=0 NormalZ=1 Radius=2.75
  constraints (2):
    c: Coincident(g0,g-3)
    c: PointOnObject(g-3,g0)
FEATURE [PartDesign::Pocket] Pocket014025005010
  Length = 7
  Sketch = -> Sketch076
  Type = 0
FEATURE [Sketcher::SketchObject] Sketch077
  ExternalGeometry = -> [Pocket014025005010]
  Placement = pos=(0,0,43.5) rot=(1,0,0;3.14159rad)
  Support = -> Pocket014025005010 [Face129]
  sketch-geometry (1):
    g0: Circle CenterX=23 CenterY=50 CenterZ=0 NormalX=0 NormalY=0 NormalZ=1 Radius=2.75
  constraints (2):
    c: Coincident(g0,g-3)
    c: PointOnObject(g-3,g0)
FEATURE [PartDesign::Pad] Pad025
  Length = 4
  Length2 = 100
  Reversed = true
  Sketch = -> Sketch077
  Type = 0
FEATURE [Part::Feature] Pad025001  label="Pad026"
  shape: bbox 101.9 x 117.7 x 55.51 mm, 172 faces (baked)
FEATURE [PartDesign::Chamfer] Chamfer018002
  Base = -> Pad025001 [Edge472]
  Size = 3.75
FEATURE [PartDesign::Chamfer] Chamfer018003
  Base = -> Chamfer018002 [Edge20]
  Size = 4
FEATURE [PartDesign::Chamfer] Chamfer018004
  Base = -> Chamfer018003 [Edge2]
  Size = 3
FEATURE [Sketcher::SketchObject] Sketch078
  ExternalGeometry = -> [Chamfer018004]
  Placement = pos=(-8.08289,4.66666,0) rot=(-0.377964,0.654654,0.654654;3.86433rad)
  Support = -> Chamfer018004 [Face49]
  sketch-geometry (2):
    g0: Circle CenterX=59.7913 CenterY=50.1 CenterZ=0 NormalX=0 NormalY=0 NormalZ=1 Radius=2
    g1: Circle CenterX=59.7913 CenterY=24.1 CenterZ=0 NormalX=0 NormalY=0 NormalZ=1 Radius=2
  constraints (4):
    c: Coincident(g0,g-3)
    c: Coincident(g1,g-4)
    c: Equal(g0,g1)
    c: Radius(g0) = 2
FEATURE [PartDesign::Pocket] Pocket014025005011
  Length = 5
  Sketch = -> Sketch078
  Type = 1
FEATURE [Sketcher::SketchObject] Sketch079
  ExternalGeometry = -> [Pocket014025005011]
  Placement = pos=(8.08289,4.66666,0) rot=(0.377964,0.654654,0.654654;2.41886rad)
  Support = -> Pocket014025005011 [Face18]
  sketch-geometry (2):
    g0: Circle CenterX=-59.7942 CenterY=50.1 CenterZ=0 NormalX=0 NormalY=0 NormalZ=1 Radius=2
    g1: Circle CenterX=-59.7942 CenterY=24.1 CenterZ=0 NormalX=0 NormalY=0 NormalZ=1 Radius=2
  constraints (4):
    c: Coincident(g0,g-3)
    c: Coincident(g1,g-4)
    c: Equal(g1,g0)
    c: Radius(g0) = 2
FEATURE [PartDesign::Pocket] Pocket014025005012
  Length = 5
  Sketch = -> Sketch079
  Type = 1
FEATURE [Sketcher::SketchObject] Sketch080
  ExternalGeometry = -> [Pocket014025005012]
  Placement = pos=(0,0,55.5) rot=(0,0,1;0rad)
  Support = -> Pocket014025005012 [Face39]
  sketch-geometry (9):
    g0: LineSegment StartX=-36 StartY=-54.6154 StartZ=0 EndX=-38.6 EndY=-54.6154 EndZ=0
    g1: LineSegment StartX=-38.6 StartY=-54.6154 StartZ=0 EndX=-42.5 EndY=-50.7154 EndZ=0
    g2: LineSegment StartX=-42.5 StartY=-50.7154 StartZ=0 EndX=-38.4008 EndY=-43.6154 EndZ=0
    g3: LineSegment StartX=-38.4008 StartY=-43.6154 StartZ=0 EndX=-35.9585 EndY=-43.6154 EndZ=0
    g4: LineSegment [constr] StartX=-42.5 StartY=-50.7154 StartZ=0 EndX=-40 EndY=-50.7154 EndZ=0
    g5: LineSegment StartX=-36 StartY=-54.6154 StartZ=0 EndX=-32.0596 EndY=-54.6154 EndZ=0
    g6: LineSegment StartX=-32.0596 StartY=-54.6154 StartZ=0 EndX=-28.0596 EndY=-50.6154 EndZ=0
    g7: LineSegment StartX=-28.0596 StartY=-50.6154 StartZ=0 EndX=-28.0596 EndY=-43.6154 EndZ=0
    g8: LineSegment StartX=-28.0596 StartY=-43.6154 StartZ=0 EndX=-35.9585 EndY=-43.6154 EndZ=0
  constraints (22):
    c: Coincident(g-5,g0)
    c: Horizontal(g0)
    c: Coincident(g0,g1)
    c: Coincident(g1,g2)
    c: Coincident(g2,g3)
    c: Coincident(g3,g-4)
    c: Horizontal(g3)
    c: Parallel(g1,g-7)
    c: Parallel(g2,g-4)
    c: Coincident(g4,g1)
    c: Coincident(g4,g-7)
    c: Horizontal(g4)
    c: DistanceX(g4) = 2.5
    c: Coincident(g0,g5)
    c: Coincident(g5,g-6)
    c: Coincident(g5,g6)
    c: Coincident(g6,g-6)
    c: Coincident(g6,g7)
    c: PointOnObject(g7,g-3)
    c: Vertical(g7)
    c: Coincident(g7,g8)
    c: Coincident(g8,g3)
FEATURE [PartDesign::Pad] Pad025002
  Length = 36
  Length2 = 100
  Reversed = true
  Sketch = -> Sketch080
  Type = 0
FEATURE [PartDesign::Chamfer] Chamfer018005
  Base = -> Pad025002 [Edge480,Edge481]
  Size = 1.7
FEATURE [Sketcher::SketchObject] Sketch081
  ExternalGeometry = -> [Chamfer018005]
  Placement = pos=(0,-54.6154,0) rot=(1,0,0;1.5708rad)
  Support = -> Chamfer018005 [Face21]
  sketch-geometry (1):
    g0: Circle CenterX=-27 CenterY=39 CenterZ=0 NormalX=0 NormalY=0 NormalZ=1 Radius=2.75
  constraints (2):
    c: Coincident(g0,g-3)
    c: Equal(g-3,g0)
FEATURE [PartDesign::Pocket] Pocket014025005013
  Length = 5
  Sketch = -> Sketch081
  Type = 1
FEATURE [Sketcher::SketchObject] Sketch082
  ExternalGeometry = -> [Pocket014025005013]
  Placement = pos=(0,-54.6154,0) rot=(1,0,0;1.5708rad)
  Support = -> Pocket014025005013 [Face21]
  sketch-geometry (1):
    g0: Circle CenterX=-27 CenterY=39 CenterZ=0 NormalX=0 NormalY=0 NormalZ=1 Radius=5
  constraints (2):
    c: Coincident(g0,g-3)
    c: Radius(g0) = 5
FEATURE [PartDesign::Pocket] Pocket014025005014
  Length = 4
  Sketch = -> Sketch082
  Type = 0
FEATURE [Sketcher::SketchObject] Sketch083
  ExternalGeometry = -> [Pocket014025005014]
  Placement = pos=(-9.91459,5.72419,0) rot=(-0.377964,0.654654,0.654654;3.86433rad)
  Support = -> Pocket014025005014 [Face2]
  sketch-geometry (6):
    g0: Circle CenterX=61.0716 CenterY=50.1 CenterZ=0 NormalX=0 NormalY=0 NormalZ=1 Radius=2.7
    g1: Circle CenterX=61.0716 CenterY=24.1 CenterZ=0 NormalX=0 NormalY=0 NormalZ=1 Radius=2.7
    g2: LineSegment [constr] StartX=61.0716 StartY=50.1 StartZ=0 EndX=61.0716 EndY=55.5 EndZ=0
    g3: LineSegment [constr] StartX=61.0716 StartY=24.1 StartZ=0 EndX=61.0716 EndY=50.1 EndZ=0
    g4: LineSegment [constr] StartX=56.9724 StartY=55.5 StartZ=0 EndX=61.0716 EndY=50.1 EndZ=0
    g5: LineSegment [constr] StartX=61.0716 StartY=50.1 StartZ=0 EndX=65.1708 EndY=55.5 EndZ=0
  constraints (15):
    c: Coincident(g2,g0)
    c: PointOnObject(g2,g-3)
    c: Vertical(g2)
    c: Coincident(g3,g1)
    c: Coincident(g3,g0)
    c: Vertical(g3)
    c: DistanceY(g2) = 5.4
    c: DistanceY(g3) = 26
    c: Radius(g0) = 2.7
    c: Equal(g0,g1)
    c: Coincident(g-3,g4)
    c: Coincident(g4,g0)
    c: Coincident(g4,g5)
    c: Coincident(g5,g-3)
    c: Equal(g5,g4)
FEATURE [PartDesign::Pocket] Pocket014025005015
  Length = 8
  Sketch = -> Sketch083
  Type = 0
FEATURE [Sketcher::SketchObject] Sketch084
  ExternalGeometry = -> [Pocket014025005015]
  Placement = pos=(-9.91459,5.72419,0) rot=(-0.377964,0.654654,0.654654;3.86433rad)
  Support = -> Pocket014025005015 [Face2]
  sketch-geometry (2):
    g0: Circle CenterX=61.0716 CenterY=50.1 CenterZ=0 NormalX=0 NormalY=0 NormalZ=1 Radius=1.7
    g1: Circle CenterX=61.0716 CenterY=24.1 CenterZ=0 NormalX=0 NormalY=0 NormalZ=1 Radius=1.7
  constraints (4):
    c: Coincident(g0,g-3)
    c: Coincident(g1,g-4)
    c: Equal(g1,g0)
    c: Radius(g0) = 1.7
FEATURE [PartDesign::Pocket] Pocket014025005016
  Length = 5
  Sketch = -> Sketch084
  Type = 1
